annotation { "Feature Type Name" : "Feature", "Feature Type Description" : "" }
export const myFeature = defineFeature(function(context is Context, id is Id, definition is map)
    precondition{}
    {
        {
            var Q0;
            Q0=qCreatedBy(makeId("Front.planeOp"),FACE);
            var sketch = newSketch(context, id + "F0", { "sketchPlane" : qUnion([Q0])});
            skLineSegment(sketch, "E0", {"start": v(0, 0) * mm, "end": v(-50.92, 0) * mm, "construction": true});
            skLineSegment(sketch, "E1", {"start": v(-59.44, 28.53) * mm, "end": v(-47.38, 28.53) * mm});
            skLineSegment(sketch, "E2", {"start": v(-47.38, 28.53) * mm, "end": v(-46.97, 28.2) * mm});
            skLineSegment(sketch, "E3", {"start": v(-46.97, 28.2) * mm, "end": v(-46.4, 28.2) * mm});
            skLineSegment(sketch, "E4", {"start": v(-46.4, 28.2) * mm, "end": v(-46.08, 27.63) * mm});
            skLineSegment(sketch, "E5", {"start": v(-46.08, 27.63) * mm, "end": v(-45.23, 27.63) * mm});
            skLineSegment(sketch, "E6", {"start": v(-45.23, 27.63) * mm, "end": v(-44.93, 27.95) * mm});
            skLineSegment(sketch, "E7", {"start": v(-44.93, 27.95) * mm, "end": v(-41.43, 27.95) * mm});
            skLineSegment(sketch, "E8", {"start": v(-41.43, 27.95) * mm, "end": v(-38.99, 27.4) * mm});
            skLineSegment(sketch, "E9", {"start": v(-38.99, 27.4) * mm, "end": v(-34.59, 27.4) * mm});
            skLineSegment(sketch, "E10", {"start": v(-34.59, 27.4) * mm, "end": v(-21.47, 25.81) * mm});
            skLineSegment(sketch, "E11", {"start": v(-21.47, 25.81) * mm, "end": v(-21.47, 24.59) * mm});
            skLineSegment(sketch, "E12", {"start": v(-21.47, 24.59) * mm, "end": v(-21.11, 24.59) * mm});
            skLineSegment(sketch, "E13", {"start": v(-21.11, 24.59) * mm, "end": v(-21.11, 25.78) * mm});
            skLineSegment(sketch, "E14", {"start": v(-21.11, 25.78) * mm, "end": v(-7.6, 24.55) * mm});
            skLineSegment(sketch, "E15", {"start": v(-7.6, 24.55) * mm, "end": v(-7.6, 23.89) * mm});
            skLineSegment(sketch, "E16", {"start": v(-7.6, 23.89) * mm, "end": v(-8.15, 23.89) * mm});
            skLineSegment(sketch, "E17", {"start": v(-8.15, 23.89) * mm, "end": v(-8.15, 21.86) * mm});
            skLineSegment(sketch, "E18", {"start": v(-8.15, 21.86) * mm, "end": v(-7.6, 21.86) * mm});
            skLineSegment(sketch, "E19", {"start": v(-7.6, 21.86) * mm, "end": v(-7.6, 21.05) * mm});
            skLineSegment(sketch, "E20", {"start": v(-7.6, 21.05) * mm, "end": v(-21.1, 20.83) * mm});
            skLineSegment(sketch, "E21", {"start": v(-21.1, 20.83) * mm, "end": v(-21.13, 22.18) * mm});
            skLineSegment(sketch, "E22", {"start": v(-21.13, 22.18) * mm, "end": v(-21.48, 22.18) * mm});
            skLineSegment(sketch, "E23", {"start": v(-21.48, 22.18) * mm, "end": v(-21.48, 21.12) * mm});
            skLineSegment(sketch, "E24", {"start": v(-21.48, 21.12) * mm, "end": v(-21.7, 20.86) * mm});
            skLineSegment(sketch, "E25", {"start": v(-21.7, 20.86) * mm, "end": v(-22.73, 20.86) * mm});
            skLineSegment(sketch, "E26", {"start": v(-22.73, 20.86) * mm, "end": v(-22.73, 20.7) * mm});
            skLineSegment(sketch, "E27", {"start": v(-22.73, 20.7) * mm, "end": v(-18.14, 17.09) * mm});
            skLineSegment(sketch, "E28", {"start": v(-18.14, 17.09) * mm, "end": v(-16.15, 17.09) * mm});
            skLineSegment(sketch, "E29", {"start": v(-16.15, 17.09) * mm, "end": v(-0.56, 15.1) * mm});
            skLineSegment(sketch, "E30", {"start": v(-0.56, 15.1) * mm, "end": v(-0.54, 13.68) * mm});
            skLineSegment(sketch, "E31", {"start": v(-0.54, 13.68) * mm, "end": v(-0.25, 13.68) * mm});
            skLineSegment(sketch, "E32", {"start": v(-0.25, 13.68) * mm, "end": v(-0.27, 15.02) * mm});
            skLineSegment(sketch, "E33", {"start": v(-0.27, 15.02) * mm, "end": v(16.38, 13.51) * mm});
            skLineSegment(sketch, "E34", {"start": v(16.38, 13.51) * mm, "end": v(16.38, 12.7) * mm});
            skLineSegment(sketch, "E35", {"start": v(16.38, 12.7) * mm, "end": v(15.82, 12.7) * mm});
            skLineSegment(sketch, "E36", {"start": v(15.82, 12.7) * mm, "end": v(15.86, 10.38) * mm});
            skLineSegment(sketch, "E37", {"start": v(15.86, 10.38) * mm, "end": v(16.35, 10.38) * mm});
            skLineSegment(sketch, "E38", {"start": v(16.35, 10.38) * mm, "end": v(16.37, 9.4) * mm});
            skLineSegment(sketch, "E39", {"start": v(16.37, 9.4) * mm, "end": v(-0.25, 9.13) * mm});
            skLineSegment(sketch, "E40", {"start": v(-0.25, 9.13) * mm, "end": v(-0.28, 10.88) * mm});
            skLineSegment(sketch, "E41", {"start": v(-0.28, 10.88) * mm, "end": v(-0.54, 10.88) * mm});
            skLineSegment(sketch, "E42", {"start": v(-0.54, 10.88) * mm, "end": v(-0.54, 9.14) * mm});
            skLineSegment(sketch, "E43", {"start": v(-0.54, 9.14) * mm, "end": v(-8.2, 9.01) * mm});
            skLineSegment(sketch, "E44", {"start": v(-8.2, 9.01) * mm, "end": v(-8.2, 8.86) * mm});
            skLineSegment(sketch, "E45", {"start": v(-8.2, 8.86) * mm, "end": v(-7.44, 8.32) * mm});
            skArc(sketch, "E46", {"start": v(-3.59, 6.94) * mm, "mid": v(-5.48, 7.72) * mm, "end": v(-7.44, 8.32) * mm});
            skFitSpline(sketch, "E47", {"points": [v(-3.59, 6.94) * mm, v(-0.35, 6.94) * mm, v(7.38, 6.77) * mm, v(22.07, 6.1) * mm, v(35.41, 5.21) * mm, v(54.7, 3.45) * mm, v(59.39, 2.97) * mm], "startDerivative": vector(30.77, 0.14) * mm, "endDerivative": vector(31.87, -3.28) * mm});
            skLineSegment(sketch, "E48", {"start": v(59.39, 2.97) * mm, "end": v(60.15, 3.97) * mm});
            skArc(sketch, "E49", {"start": v(69.05, 3.31) * mm, "mid": v(64.61, 3.8) * mm, "end": v(60.15, 3.97) * mm});
            skLineSegment(sketch, "E50", {"start": v(69.05, 3.31) * mm, "end": v(67.9, 2.36) * mm});
            skLineSegment(sketch, "E51", {"start": v(67.9, 2.36) * mm, "end": v(64.73, 2.36) * mm});
            skArc(sketch, "E52", {"start": v(65.12, 0) * mm, "mid": v(65.03, 1.2) * mm, "end": v(64.73, 2.36) * mm});
            skLineSegment(sketch, "E53", {"start": v(-9.54, 23.56) * mm, "end": v(-9.54, 22.25) * mm});
            skLineSegment(sketch, "E54", {"start": v(-9.54, 22.25) * mm, "end": v(-13.93, 22.34) * mm});
            skLineSegment(sketch, "E55", {"start": v(-13.93, 22.34) * mm, "end": v(-13.9, 23.67) * mm});
            skLineSegment(sketch, "E56", {"start": v(-13.9, 23.67) * mm, "end": v(-9.54, 23.56) * mm});
            skLineSegment(sketch, "E57", {"start": v(-59.44, 28.53) * mm, "end": v(-59.44, 26.8) * mm});
            skLineSegment(sketch, "E58", {"start": v(-59.44, 26.8) * mm, "end": v(-59, 26.48) * mm});
            skLineSegment(sketch, "E59", {"start": v(-59, 26.48) * mm, "end": v(-58.94, 22.25) * mm});
            skLineSegment(sketch, "E60", {"start": v(-58.94, 22.25) * mm, "end": v(-59.44, 21.63) * mm});
            skLineSegment(sketch, "E61", {"start": v(-59.44, 21.63) * mm, "end": v(-59.47, 19.98) * mm});
            skLineSegment(sketch, "E62", {"start": v(-59.47, 19.98) * mm, "end": v(-47.36, 19.98) * mm});
            skLineSegment(sketch, "E63", {"start": v(-47.36, 19.98) * mm, "end": v(-47.03, 20.38) * mm});
            skLineSegment(sketch, "E64", {"start": v(-47.03, 20.38) * mm, "end": v(-46.32, 20.36) * mm});
            skLineSegment(sketch, "E65", {"start": v(-46.32, 20.36) * mm, "end": v(-45.77, 21.66) * mm});
            skLineSegment(sketch, "E66", {"start": v(-45.77, 21.66) * mm, "end": v(-45.07, 21.64) * mm});
            skLineSegment(sketch, "E67", {"start": v(-45.07, 21.64) * mm, "end": v(-45.04, 19.83) * mm});
            skLineSegment(sketch, "E68", {"start": v(-45.04, 19.83) * mm, "end": v(-44.78, 19.57) * mm});
            skLineSegment(sketch, "E69", {"start": v(-44.78, 19.57) * mm, "end": v(-41.37, 19.5) * mm});
            skLineSegment(sketch, "E70", {"start": v(-41.37, 19.5) * mm, "end": v(-40.25, 20.53) * mm});
            skLineSegment(sketch, "E71", {"start": v(-40.25, 20.53) * mm, "end": v(-33.73, 20.53) * mm});
            skLineSegment(sketch, "E72", {"start": v(-33.73, 20.53) * mm, "end": v(-33.68, 17.4) * mm});
            skLineSegment(sketch, "E73", {"start": v(-33.68, 17.4) * mm, "end": v(-39.86, 17.3) * mm});
            skLineSegment(sketch, "E74", {"start": v(-39.86, 17.3) * mm, "end": v(-40.9, 17.79) * mm});
            skLineSegment(sketch, "E75", {"start": v(-40.9, 17.79) * mm, "end": v(-41.73, 17.8) * mm});
            skLineSegment(sketch, "E76", {"start": v(-41.73, 17.8) * mm, "end": v(-41.99, 18.08) * mm});
            skLineSegment(sketch, "E77", {"start": v(-41.99, 18.08) * mm, "end": v(-55.95, 18.08) * mm});
            skLineSegment(sketch, "E78", {"start": v(-55.95, 18.08) * mm, "end": v(-56.22, 17.8) * mm});
            skLineSegment(sketch, "E79", {"start": v(-56.22, 17.8) * mm, "end": v(-56.2, 16.23) * mm});
            skLineSegment(sketch, "E80", {"start": v(-56.2, 16.23) * mm, "end": v(-55.86, 15.92) * mm});
            skLineSegment(sketch, "E81", {"start": v(-55.86, 15.92) * mm, "end": v(-55.77, 10.73) * mm});
            skLineSegment(sketch, "E82", {"start": v(-55.77, 10.73) * mm, "end": v(-56.18, 10.26) * mm});
            skLineSegment(sketch, "E83", {"start": v(-56.18, 10.26) * mm, "end": v(-56.18, 8.68) * mm});
            skLineSegment(sketch, "E84", {"start": v(-56.18, 8.68) * mm, "end": v(-55.89, 8.3) * mm});
            skLineSegment(sketch, "E85", {"start": v(-55.89, 8.3) * mm, "end": v(-42.04, 8.3) * mm});
            skLineSegment(sketch, "E86", {"start": v(-42.04, 8.3) * mm, "end": v(-41.71, 8.68) * mm});
            skLineSegment(sketch, "E87", {"start": v(-41.71, 8.68) * mm, "end": v(-40.93, 8.66) * mm});
            skLineSegment(sketch, "E88", {"start": v(-40.93, 8.66) * mm, "end": v(-40.27, 10.14) * mm});
            skLineSegment(sketch, "E89", {"start": v(-40.27, 10.14) * mm, "end": v(-39.56, 10.12) * mm});
            skLineSegment(sketch, "E90", {"start": v(-39.56, 10.12) * mm, "end": v(-39.53, 8.18) * mm});
            skLineSegment(sketch, "E91", {"start": v(-39.53, 8.18) * mm, "end": v(-39.2, 7.85) * mm});
            skLineSegment(sketch, "E92", {"start": v(-39.2, 7.85) * mm, "end": v(-35.01, 7.92) * mm});
            skLineSegment(sketch, "E93", {"start": v(-35.01, 7.92) * mm, "end": v(-33.69, 8.84) * mm});
            skLineSegment(sketch, "E94", {"start": v(-33.69, 8.84) * mm, "end": v(-33.65, 6.55) * mm});
            skLineSegment(sketch, "E95", {"start": v(-33.65, 6.55) * mm, "end": v(-34.72, 5.87) * mm});
            skArc(sketch, "E96", {"start": v(-34.72, 5.87) * mm, "mid": v(-39.46, 5.43) * mm, "end": v(-44.17, 4.85) * mm});
            skLineSegment(sketch, "E97", {"start": v(-44.17, 4.85) * mm, "end": v(-45.81, 5.4) * mm});
            skLineSegment(sketch, "E98", {"start": v(-45.81, 5.4) * mm, "end": v(-50.78, 5.4) * mm});
            skLineSegment(sketch, "E99", {"start": v(-50.78, 5.4) * mm, "end": v(-50.78, 4.85) * mm});
            skLineSegment(sketch, "E100", {"start": v(-50.78, 4.85) * mm, "end": v(-49.68, 4.3) * mm});
            skLineSegment(sketch, "E101", {"start": v(-49.68, 4.3) * mm, "end": v(-50.4, 4.15) * mm});
            skArc(sketch, "E102", {"start": v(-50.4, 4.15) * mm, "mid": v(-50.8, 2.1) * mm, "end": v(-50.92, 0) * mm});
            skLineSegment(sketch, "E103", {"start": v(-55.97, 26.17) * mm, "end": v(-53.15, 26.17) * mm});
            skLineSegment(sketch, "E104", {"start": v(-53.15, 26.17) * mm, "end": v(-53.15, 22.48) * mm});
            skLineSegment(sketch, "E105", {"start": v(-53.15, 22.48) * mm, "end": v(-56, 22.48) * mm});
            skLineSegment(sketch, "E106", {"start": v(-56, 22.48) * mm, "end": v(-55.97, 26.17) * mm});
            skLineSegment(sketch, "E107", {"start": v(-52.12, 15.28) * mm, "end": v(-48.82, 15.28) * mm});
            skLineSegment(sketch, "E108", {"start": v(-48.82, 15.28) * mm, "end": v(-48.82, 11.05) * mm});
            skLineSegment(sketch, "E109", {"start": v(-48.82, 11.05) * mm, "end": v(-52.12, 11.05) * mm});
            skLineSegment(sketch, "E110", {"start": v(-52.12, 11.05) * mm, "end": v(-52.12, 15.28) * mm});
            skLineSegment(sketch, "E111", {"start": v(8.86, 12.6) * mm, "end": v(14.27, 12.35) * mm});
            skLineSegment(sketch, "E112", {"start": v(14.27, 12.35) * mm, "end": v(14.3, 10.92) * mm});
            skLineSegment(sketch, "E113", {"start": v(14.3, 10.92) * mm, "end": v(8.89, 11.02) * mm});
            skLineSegment(sketch, "E114", {"start": v(8.89, 11.02) * mm, "end": v(8.86, 12.6) * mm});
            skLineSegment(sketch, "E115.MirrorCS", {"start": v(-0.28, -10.88) * mm, "end": v(-0.54, -10.88) * mm});
            skLineSegment(sketch, "E116.MirrorCS", {"start": v(-21.13, -22.18) * mm, "end": v(-21.48, -22.18) * mm});
            skLineSegment(sketch, "E117.MirrorCS", {"start": v(-0.54, -13.68) * mm, "end": v(-0.25, -13.68) * mm});
            skLineSegment(sketch, "E118.MirrorCS", {"start": v(-0.25, -9.13) * mm, "end": v(-0.28, -10.88) * mm});
            skLineSegment(sketch, "E119.MirrorCS", {"start": v(-0.56, -15.1) * mm, "end": v(-0.54, -13.68) * mm});
            skLineSegment(sketch, "E120.MirrorCS", {"start": v(-8.15, -21.86) * mm, "end": v(-7.6, -21.86) * mm});
            skLineSegment(sketch, "E121.MirrorCS", {"start": v(-21.48, -22.18) * mm, "end": v(-21.48, -21.12) * mm});
            skLineSegment(sketch, "E122.MirrorCS", {"start": v(-0.25, -13.68) * mm, "end": v(-0.27, -15.02) * mm});
            skLineSegment(sketch, "E123.MirrorCS", {"start": v(-21.7, -20.86) * mm, "end": v(-22.73, -20.86) * mm});
            skLineSegment(sketch, "E124.MirrorCS", {"start": v(-0.54, -10.88) * mm, "end": v(-0.54, -9.14) * mm});
            skLineSegment(sketch, "E125.MirrorCS", {"start": v(-55.95, -18.08) * mm, "end": v(-56.22, -17.8) * mm});
            skLineSegment(sketch, "E126.MirrorCS", {"start": v(16.35, -10.38) * mm, "end": v(16.37, -9.4) * mm});
            skLineSegment(sketch, "E127.MirrorCS", {"start": v(15.86, -10.38) * mm, "end": v(16.35, -10.38) * mm});
            skLineSegment(sketch, "E128.MirrorCS", {"start": v(-21.1, -20.83) * mm, "end": v(-21.13, -22.18) * mm});
            skLineSegment(sketch, "E129.MirrorCS", {"start": v(-56.22, -17.8) * mm, "end": v(-56.2, -16.23) * mm});
            skLineSegment(sketch, "E130.MirrorCS", {"start": v(-47.36, -19.98) * mm, "end": v(-47.03, -20.38) * mm});
            skLineSegment(sketch, "E131.MirrorCS", {"start": v(-45.04, -19.83) * mm, "end": v(-44.78, -19.57) * mm});
            skLineSegment(sketch, "E132.MirrorCS", {"start": v(-56.18, -8.68) * mm, "end": v(-55.89, -8.3) * mm});
            skLineSegment(sketch, "E133.MirrorCS", {"start": v(15.82, -12.7) * mm, "end": v(15.86, -10.38) * mm});
            skLineSegment(sketch, "E134.MirrorCS", {"start": v(-56.2, -16.23) * mm, "end": v(-55.86, -15.92) * mm});
            skLineSegment(sketch, "E135.MirrorCS", {"start": v(59.39, -2.97) * mm, "end": v(60.15, -3.97) * mm});
            skLineSegment(sketch, "E136.MirrorCS", {"start": v(-39.53, -8.18) * mm, "end": v(-39.2, -7.85) * mm});
            skLineSegment(sketch, "E137.MirrorCS", {"start": v(-21.48, -21.12) * mm, "end": v(-21.7, -20.86) * mm});
            skLineSegment(sketch, "E138.MirrorCS", {"start": v(-8.15, -23.89) * mm, "end": v(-8.15, -21.86) * mm});
            skLineSegment(sketch, "E139.MirrorCS", {"start": v(-7.6, -21.86) * mm, "end": v(-7.6, -21.05) * mm});
            skLineSegment(sketch, "E140.MirrorCS", {"start": v(-22.73, -20.86) * mm, "end": v(-22.73, -20.7) * mm});
            skLineSegment(sketch, "E141.MirrorCS", {"start": v(-45.07, -21.64) * mm, "end": v(-45.04, -19.83) * mm});
            skLineSegment(sketch, "E142.MirrorCS", {"start": v(-56.18, -10.26) * mm, "end": v(-56.18, -8.68) * mm});
            skLineSegment(sketch, "E143.MirrorCS", {"start": v(-46.32, -20.36) * mm, "end": v(-45.77, -21.66) * mm});
            skArc(sketch, "E144.MirrorCS", {"start": v(-3.59, -6.94) * mm, "mid": v(-5.48, -7.72) * mm, "end": v(-7.44, -8.32) * mm});
            skLineSegment(sketch, "E145.MirrorCS", {"start": v(-8.2, -8.86) * mm, "end": v(-7.44, -8.32) * mm});
            skLineSegment(sketch, "E146.MirrorCS", {"start": v(-40.9, -17.79) * mm, "end": v(-41.73, -17.8) * mm});
            skLineSegment(sketch, "E147.MirrorCS", {"start": v(-45.77, -21.66) * mm, "end": v(-45.07, -21.64) * mm});
            skLineSegment(sketch, "E148.MirrorCS", {"start": v(16.38, -13.51) * mm, "end": v(16.38, -12.7) * mm});
            skLineSegment(sketch, "E149.MirrorCS", {"start": v(-7.6, -23.89) * mm, "end": v(-8.15, -23.89) * mm});
            skLineSegment(sketch, "E150.MirrorCS", {"start": v(-47.03, -20.38) * mm, "end": v(-46.32, -20.36) * mm});
            skLineSegment(sketch, "E151.MirrorCS", {"start": v(-8.2, -9.01) * mm, "end": v(-8.2, -8.86) * mm});
            skLineSegment(sketch, "E152.MirrorCS", {"start": v(-41.73, -17.8) * mm, "end": v(-41.99, -18.08) * mm});
            skLineSegment(sketch, "E153.MirrorCS", {"start": v(-21.47, -24.59) * mm, "end": v(-21.11, -24.59) * mm});
            skLineSegment(sketch, "E154.MirrorCS", {"start": v(-40.27, -10.14) * mm, "end": v(-39.56, -10.12) * mm});
            skLineSegment(sketch, "E155.MirrorCS", {"start": v(16.38, -12.7) * mm, "end": v(15.82, -12.7) * mm});
            skLineSegment(sketch, "E156.MirrorCS", {"start": v(-39.86, -17.3) * mm, "end": v(-40.9, -17.79) * mm});
            skLineSegment(sketch, "E157.MirrorCS", {"start": v(-46.97, -28.2) * mm, "end": v(-46.4, -28.2) * mm});
            skLineSegment(sketch, "E158.MirrorCS", {"start": v(-45.23, -27.63) * mm, "end": v(-44.93, -27.95) * mm});
            skLineSegment(sketch, "E159.MirrorCS", {"start": v(-33.69, -8.84) * mm, "end": v(-33.65, -6.55) * mm});
            skLineSegment(sketch, "E160.MirrorCS", {"start": v(-52.12, -11.05) * mm, "end": v(-52.12, -15.28) * mm});
            skLineSegment(sketch, "E161.MirrorCS", {"start": v(-9.54, -22.25) * mm, "end": v(-13.93, -22.34) * mm});
            skArc(sketch, "E162.MirrorCS", {"start": v(-50.4, -4.15) * mm, "mid": v(-50.8, -2.1) * mm, "end": v(-50.92, 0) * mm});
            skLineSegment(sketch, "E163.MirrorCS", {"start": v(-42.04, -8.3) * mm, "end": v(-41.71, -8.68) * mm});
            skLineSegment(sketch, "E164.MirrorCS", {"start": v(-41.37, -19.5) * mm, "end": v(-40.25, -20.53) * mm});
            skLineSegment(sketch, "E165.MirrorCS", {"start": v(-7.6, -24.55) * mm, "end": v(-7.6, -23.89) * mm});
            skLineSegment(sketch, "E166.MirrorCS", {"start": v(-44.78, -19.57) * mm, "end": v(-41.37, -19.5) * mm});
            skLineSegment(sketch, "E167.MirrorCS", {"start": v(-49.68, -4.3) * mm, "end": v(-50.4, -4.15) * mm});
            skLineSegment(sketch, "E168.MirrorCS", {"start": v(-9.54, -23.56) * mm, "end": v(-9.54, -22.25) * mm});
            skLineSegment(sketch, "E169.MirrorCS", {"start": v(-33.65, -6.55) * mm, "end": v(-34.72, -5.87) * mm});
            skLineSegment(sketch, "E170.MirrorCS", {"start": v(-35.01, -7.92) * mm, "end": v(-33.69, -8.84) * mm});
            skLineSegment(sketch, "E171.MirrorCS", {"start": v(-48.82, -11.05) * mm, "end": v(-52.12, -11.05) * mm});
            skLineSegment(sketch, "E172.MirrorCS", {"start": v(-59.44, -21.63) * mm, "end": v(-59.47, -19.98) * mm});
            skLineSegment(sketch, "E173.MirrorCS", {"start": v(-21.11, -24.59) * mm, "end": v(-21.11, -25.78) * mm});
            skLineSegment(sketch, "E174.MirrorCS", {"start": v(-13.93, -22.34) * mm, "end": v(-13.9, -23.67) * mm});
            skLineSegment(sketch, "E175.MirrorCS", {"start": v(-55.97, -26.17) * mm, "end": v(-53.15, -26.17) * mm});
            skLineSegment(sketch, "E176.MirrorCS", {"start": v(-41.71, -8.68) * mm, "end": v(-40.93, -8.66) * mm});
            skLineSegment(sketch, "E177.MirrorCS", {"start": v(-50.78, -4.85) * mm, "end": v(-49.68, -4.3) * mm});
            skLineSegment(sketch, "E178.MirrorCS", {"start": v(-55.77, -10.73) * mm, "end": v(-56.18, -10.26) * mm});
            skLineSegment(sketch, "E179.MirrorCS", {"start": v(-59, -26.48) * mm, "end": v(-58.94, -22.25) * mm});
            skLineSegment(sketch, "E180.MirrorCS", {"start": v(69.05, -3.31) * mm, "end": v(67.9, -2.36) * mm});
            skLineSegment(sketch, "E181.MirrorCS", {"start": v(-22.73, -20.7) * mm, "end": v(-18.14, -17.09) * mm});
            skLineSegment(sketch, "E182.MirrorCS", {"start": v(-52.12, -15.28) * mm, "end": v(-48.82, -15.28) * mm});
            skLineSegment(sketch, "E183.MirrorCS", {"start": v(8.89, -11.02) * mm, "end": v(8.86, -12.6) * mm});
            skLineSegment(sketch, "E184.MirrorCS", {"start": v(-59.44, -28.53) * mm, "end": v(-59.44, -26.8) * mm});
            skLineSegment(sketch, "E185.MirrorCS", {"start": v(-18.14, -17.09) * mm, "end": v(-16.15, -17.09) * mm});
            skLineSegment(sketch, "E186.MirrorCS", {"start": v(-45.81, -5.4) * mm, "end": v(-50.78, -5.4) * mm});
            skLineSegment(sketch, "E187.MirrorCS", {"start": v(-58.94, -22.25) * mm, "end": v(-59.44, -21.63) * mm});
            skLineSegment(sketch, "E188.MirrorCS", {"start": v(67.9, -2.36) * mm, "end": v(64.73, -2.36) * mm});
            skLineSegment(sketch, "E189.MirrorCS", {"start": v(-39.2, -7.85) * mm, "end": v(-35.01, -7.92) * mm});
            skLineSegment(sketch, "E190.MirrorCS", {"start": v(-44.17, -4.85) * mm, "end": v(-45.81, -5.4) * mm});
            skLineSegment(sketch, "E191.MirrorCS", {"start": v(-48.82, -15.28) * mm, "end": v(-48.82, -11.05) * mm});
            skLineSegment(sketch, "E192.MirrorCS", {"start": v(14.27, -12.35) * mm, "end": v(14.3, -10.92) * mm});
            skLineSegment(sketch, "E193.MirrorCS", {"start": v(-13.9, -23.67) * mm, "end": v(-9.54, -23.56) * mm});
            skLineSegment(sketch, "E194.MirrorCS", {"start": v(-53.15, -26.17) * mm, "end": v(-53.15, -22.48) * mm});
            skLineSegment(sketch, "E195.MirrorCS", {"start": v(-33.73, -20.53) * mm, "end": v(-33.68, -17.4) * mm});
            skLineSegment(sketch, "E196.MirrorCS", {"start": v(-56, -22.48) * mm, "end": v(-55.97, -26.17) * mm});
            skLineSegment(sketch, "E197.MirrorCS", {"start": v(-40.93, -8.66) * mm, "end": v(-40.27, -10.14) * mm});
            skLineSegment(sketch, "E198.MirrorCS", {"start": v(-39.56, -10.12) * mm, "end": v(-39.53, -8.18) * mm});
            skLineSegment(sketch, "E199.MirrorCS", {"start": v(-50.78, -5.4) * mm, "end": v(-50.78, -4.85) * mm});
            skLineSegment(sketch, "E200.MirrorCS", {"start": v(-53.15, -22.48) * mm, "end": v(-56, -22.48) * mm});
            skLineSegment(sketch, "E201.MirrorCS", {"start": v(-59.44, -26.8) * mm, "end": v(-59, -26.48) * mm});
            skLineSegment(sketch, "E202.MirrorCS", {"start": v(-21.47, -25.81) * mm, "end": v(-21.47, -24.59) * mm});
            skLineSegment(sketch, "E203.MirrorCS", {"start": v(-44.93, -27.95) * mm, "end": v(-41.43, -27.95) * mm});
            skLineSegment(sketch, "E204.MirrorCS", {"start": v(-47.38, -28.53) * mm, "end": v(-46.97, -28.2) * mm});
            skLineSegment(sketch, "E205.MirrorCS", {"start": v(-46.08, -27.63) * mm, "end": v(-45.23, -27.63) * mm});
            skLineSegment(sketch, "E206.MirrorCS", {"start": v(-46.4, -28.2) * mm, "end": v(-46.08, -27.63) * mm});
            skLineSegment(sketch, "E207.MirrorCS", {"start": v(-41.43, -27.95) * mm, "end": v(-38.99, -27.4) * mm});
            skArc(sketch, "E208.MirrorCS", {"start": v(65.12, 0) * mm, "mid": v(65.03, -1.2) * mm, "end": v(64.73, -2.36) * mm});
            skLineSegment(sketch, "E209.MirrorCS", {"start": v(-0.54, -9.14) * mm, "end": v(-8.2, -9.01) * mm});
            skLineSegment(sketch, "E210.MirrorCS", {"start": v(-59.47, -19.98) * mm, "end": v(-47.36, -19.98) * mm});
            skLineSegment(sketch, "E211.MirrorCS", {"start": v(-21.11, -25.78) * mm, "end": v(-7.6, -24.55) * mm});
            skLineSegment(sketch, "E212.MirrorCS", {"start": v(-55.89, -8.3) * mm, "end": v(-42.04, -8.3) * mm});
            skFitSpline(sketch, "E213.MirrorCS", {"points": [v(-3.59, -6.94) * mm, v(-0.35, -6.94) * mm, v(7.38, -6.77) * mm, v(22.07, -6.1) * mm, v(35.41, -5.21) * mm, v(54.7, -3.45) * mm, v(59.39, -2.97) * mm], "startDerivative": vector(30.77, -0.14) * mm, "endDerivative": vector(31.87, 3.28) * mm});
            skLineSegment(sketch, "E214.MirrorCS", {"start": v(8.86, -12.6) * mm, "end": v(14.27, -12.35) * mm});
            skLineSegment(sketch, "E215.MirrorCS", {"start": v(-16.15, -17.09) * mm, "end": v(-0.56, -15.1) * mm});
            skLineSegment(sketch, "E216.MirrorCS", {"start": v(-41.99, -18.08) * mm, "end": v(-55.95, -18.08) * mm});
            skLineSegment(sketch, "E217.MirrorCS", {"start": v(16.37, -9.4) * mm, "end": v(-0.25, -9.13) * mm});
            skLineSegment(sketch, "E218.MirrorCS", {"start": v(-7.6, -21.05) * mm, "end": v(-21.1, -20.83) * mm});
            skLineSegment(sketch, "E219.MirrorCS", {"start": v(-40.25, -20.53) * mm, "end": v(-33.73, -20.53) * mm});
            skLineSegment(sketch, "E220.MirrorCS", {"start": v(-33.68, -17.4) * mm, "end": v(-39.86, -17.3) * mm});
            skLineSegment(sketch, "E221.MirrorCS", {"start": v(-34.59, -27.4) * mm, "end": v(-21.47, -25.81) * mm});
            skLineSegment(sketch, "E222.MirrorCS", {"start": v(-38.99, -27.4) * mm, "end": v(-34.59, -27.4) * mm});
            skLineSegment(sketch, "E223.MirrorCS", {"start": v(14.3, -10.92) * mm, "end": v(8.89, -11.02) * mm});
            skLineSegment(sketch, "E224.MirrorCS", {"start": v(-59.44, -28.53) * mm, "end": v(-47.38, -28.53) * mm});
            skLineSegment(sketch, "E225.MirrorCS", {"start": v(-55.86, -15.92) * mm, "end": v(-55.77, -10.73) * mm});
            skLineSegment(sketch, "E226.MirrorCS", {"start": v(-0.27, -15.02) * mm, "end": v(16.38, -13.51) * mm});
            skArc(sketch, "E227.MirrorCS", {"start": v(69.05, -3.31) * mm, "mid": v(64.61, -3.8) * mm, "end": v(60.15, -3.97) * mm});
            skArc(sketch, "E228.MirrorCS", {"start": v(-34.72, -5.87) * mm, "mid": v(-39.46, -5.43) * mm, "end": v(-44.17, -4.85) * mm});
            skSolve(sketch);
        }
        {
            var Q0;
            Q0=makeQuery(id+"F0.imprint","IMPRINT",FACE,{"disambiguationData":[TD([[makeQuery(id+"F0.imprint","IMPRINT",EDGE,{"derivedFrom":sQuery(id+"F0.wireOp",EDGE,"E1")}),-1.0]])]});
            extrude(context, id + "F1", {"entities" : qUnion([Q0]), "depth" : 2 * mm, "offsetDistance" : 25 * mm});
        }
        {
            var Q0;
            Q0=makeQuery(id+"F1.opExtrude","SWEPT_BODY",BODY,{"disambiguationData":[OSD([sQuery(id+"F0.wireOp",EDGE,"E1"),sQuery(id+"F0.wireOp",EDGE,"E2"),sQuery(id+"F0.wireOp",EDGE,"E3"),sQuery(id+"F0.wireOp",EDGE,"E4"),sQuery(id+"F0.wireOp",EDGE,"E5"),sQuery(id+"F0.wireOp",EDGE,"E6"),sQuery(id+"F0.wireOp",EDGE,"E7"),sQuery(id+"F0.wireOp",EDGE,"E8"),sQuery(id+"F0.wireOp",EDGE,"E9"),sQuery(id+"F0.wireOp",EDGE,"E10"),sQuery(id+"F0.wireOp",EDGE,"E11"),sQuery(id+"F0.wireOp",EDGE,"E12"),sQuery(id+"F0.wireOp",EDGE,"E13"),sQuery(id+"F0.wireOp",EDGE,"E14"),sQuery(id+"F0.wireOp",EDGE,"E15"),sQuery(id+"F0.wireOp",EDGE,"E16"),sQuery(id+"F0.wireOp",EDGE,"E17"),sQuery(id+"F0.wireOp",EDGE,"E18"),sQuery(id+"F0.wireOp",EDGE,"E19"),sQuery(id+"F0.wireOp",EDGE,"E20"),sQuery(id+"F0.wireOp",EDGE,"E21"),sQuery(id+"F0.wireOp",EDGE,"E22"),sQuery(id+"F0.wireOp",EDGE,"E23"),sQuery(id+"F0.wireOp",EDGE,"E24"),sQuery(id+"F0.wireOp",EDGE,"E25"),sQuery(id+"F0.wireOp",EDGE,"E26"),sQuery(id+"F0.wireOp",EDGE,"E27"),sQuery(id+"F0.wireOp",EDGE,"E28"),sQuery(id+"F0.wireOp",EDGE,"E29"),sQuery(id+"F0.wireOp",EDGE,"E30"),sQuery(id+"F0.wireOp",EDGE,"E31"),sQuery(id+"F0.wireOp",EDGE,"E32"),sQuery(id+"F0.wireOp",EDGE,"E33"),sQuery(id+"F0.wireOp",EDGE,"E34"),sQuery(id+"F0.wireOp",EDGE,"E35"),sQuery(id+"F0.wireOp",EDGE,"E36"),sQuery(id+"F0.wireOp",EDGE,"E37"),sQuery(id+"F0.wireOp",EDGE,"E38"),sQuery(id+"F0.wireOp",EDGE,"E39"),sQuery(id+"F0.wireOp",EDGE,"E40"),sQuery(id+"F0.wireOp",EDGE,"E41"),sQuery(id+"F0.wireOp",EDGE,"E42"),sQuery(id+"F0.wireOp",EDGE,"E43"),sQuery(id+"F0.wireOp",EDGE,"E44"),sQuery(id+"F0.wireOp",EDGE,"E45"),sQuery(id+"F0.wireOp",EDGE,"E46"),sQuery(id+"F0.wireOp",EDGE,"E47"),sQuery(id+"F0.wireOp",EDGE,"E48"),sQuery(id+"F0.wireOp",EDGE,"E49"),sQuery(id+"F0.wireOp",EDGE,"E50"),sQuery(id+"F0.wireOp",EDGE,"E51"),sQuery(id+"F0.wireOp",EDGE,"E52"),sQuery(id+"F0.wireOp",EDGE,"E53"),sQuery(id+"F0.wireOp",EDGE,"E54"),sQuery(id+"F0.wireOp",EDGE,"E55"),sQuery(id+"F0.wireOp",EDGE,"E56"),sQuery(id+"F0.wireOp",EDGE,"E57"),sQuery(id+"F0.wireOp",EDGE,"E58"),sQuery(id+"F0.wireOp",EDGE,"E59"),sQuery(id+"F0.wireOp",EDGE,"E60"),sQuery(id+"F0.wireOp",EDGE,"E61"),sQuery(id+"F0.wireOp",EDGE,"E62"),sQuery(id+"F0.wireOp",EDGE,"E63"),sQuery(id+"F0.wireOp",EDGE,"E64"),sQuery(id+"F0.wireOp",EDGE,"E65"),sQuery(id+"F0.wireOp",EDGE,"E66"),sQuery(id+"F0.wireOp",EDGE,"E67"),sQuery(id+"F0.wireOp",EDGE,"E68"),sQuery(id+"F0.wireOp",EDGE,"E69"),sQuery(id+"F0.wireOp",EDGE,"E70"),sQuery(id+"F0.wireOp",EDGE,"E71"),sQuery(id+"F0.wireOp",EDGE,"E72"),sQuery(id+"F0.wireOp",EDGE,"E73"),sQuery(id+"F0.wireOp",EDGE,"E74"),sQuery(id+"F0.wireOp",EDGE,"E75"),sQuery(id+"F0.wireOp",EDGE,"E76"),sQuery(id+"F0.wireOp",EDGE,"E77"),sQuery(id+"F0.wireOp",EDGE,"E78"),sQuery(id+"F0.wireOp",EDGE,"E79"),sQuery(id+"F0.wireOp",EDGE,"E80"),sQuery(id+"F0.wireOp",EDGE,"E81"),sQuery(id+"F0.wireOp",EDGE,"E82"),sQuery(id+"F0.wireOp",EDGE,"E83"),sQuery(id+"F0.wireOp",EDGE,"E84"),sQuery(id+"F0.wireOp",EDGE,"E85"),sQuery(id+"F0.wireOp",EDGE,"E86"),sQuery(id+"F0.wireOp",EDGE,"E87"),sQuery(id+"F0.wireOp",EDGE,"E88"),sQuery(id+"F0.wireOp",EDGE,"E89"),sQuery(id+"F0.wireOp",EDGE,"E90"),sQuery(id+"F0.wireOp",EDGE,"E91"),sQuery(id+"F0.wireOp",EDGE,"E92"),sQuery(id+"F0.wireOp",EDGE,"E93"),sQuery(id+"F0.wireOp",EDGE,"E94"),sQuery(id+"F0.wireOp",EDGE,"E95"),sQuery(id+"F0.wireOp",EDGE,"E96"),sQuery(id+"F0.wireOp",EDGE,"E97"),sQuery(id+"F0.wireOp",EDGE,"E98"),sQuery(id+"F0.wireOp",EDGE,"E99"),sQuery(id+"F0.wireOp",EDGE,"E100"),sQuery(id+"F0.wireOp",EDGE,"E101"),sQuery(id+"F0.wireOp",EDGE,"E102"),sQuery(id+"F0.wireOp",EDGE,"E103"),sQuery(id+"F0.wireOp",EDGE,"E104"),sQuery(id+"F0.wireOp",EDGE,"E105"),sQuery(id+"F0.wireOp",EDGE,"E106"),sQuery(id+"F0.wireOp",EDGE,"E107"),sQuery(id+"F0.wireOp",EDGE,"E108"),sQuery(id+"F0.wireOp",EDGE,"E109"),sQuery(id+"F0.wireOp",EDGE,"E110"),sQuery(id+"F0.wireOp",EDGE,"E111"),sQuery(id+"F0.wireOp",EDGE,"E112"),sQuery(id+"F0.wireOp",EDGE,"E113"),sQuery(id+"F0.wireOp",EDGE,"E114"),sQuery(id+"F0.wireOp",EDGE,"E115.MirrorCS"),sQuery(id+"F0.wireOp",EDGE,"E116.MirrorCS"),sQuery(id+"F0.wireOp",EDGE,"E117.MirrorCS"),sQuery(id+"F0.wireOp",EDGE,"E118.MirrorCS"),sQuery(id+"F0.wireOp",EDGE,"E119.MirrorCS"),sQuery(id+"F0.wireOp",EDGE,"E120.MirrorCS"),sQuery(id+"F0.wireOp",EDGE,"E121.MirrorCS"),sQuery(id+"F0.wireOp",EDGE,"E122.MirrorCS"),sQuery(id+"F0.wireOp",EDGE,"E123.MirrorCS"),sQuery(id+"F0.wireOp",EDGE,"E124.MirrorCS"),sQuery(id+"F0.wireOp",EDGE,"E125.MirrorCS"),sQuery(id+"F0.wireOp",EDGE,"E126.MirrorCS"),sQuery(id+"F0.wireOp",EDGE,"E127.MirrorCS"),sQuery(id+"F0.wireOp",EDGE,"E128.MirrorCS"),sQuery(id+"F0.wireOp",EDGE,"E129.MirrorCS"),sQuery(id+"F0.wireOp",EDGE,"E130.MirrorCS"),sQuery(id+"F0.wireOp",EDGE,"E131.MirrorCS"),sQuery(id+"F0.wireOp",EDGE,"E132.MirrorCS"),sQuery(id+"F0.wireOp",EDGE,"E133.MirrorCS"),sQuery(id+"F0.wireOp",EDGE,"E134.MirrorCS"),sQuery(id+"F0.wireOp",EDGE,"E135.MirrorCS"),sQuery(id+"F0.wireOp",EDGE,"E136.MirrorCS"),sQuery(id+"F0.wireOp",EDGE,"E137.MirrorCS"),sQuery(id+"F0.wireOp",EDGE,"E138.MirrorCS"),sQuery(id+"F0.wireOp",EDGE,"E139.MirrorCS"),sQuery(id+"F0.wireOp",EDGE,"E140.MirrorCS"),sQuery(id+"F0.wireOp",EDGE,"E141.MirrorCS"),sQuery(id+"F0.wireOp",EDGE,"E142.MirrorCS"),sQuery(id+"F0.wireOp",EDGE,"E143.MirrorCS"),sQuery(id+"F0.wireOp",EDGE,"E144.MirrorCS"),sQuery(id+"F0.wireOp",EDGE,"E145.MirrorCS"),sQuery(id+"F0.wireOp",EDGE,"E146.MirrorCS"),sQuery(id+"F0.wireOp",EDGE,"E147.MirrorCS"),sQuery(id+"F0.wireOp",EDGE,"E148.MirrorCS"),sQuery(id+"F0.wireOp",EDGE,"E149.MirrorCS"),sQuery(id+"F0.wireOp",EDGE,"E150.MirrorCS"),sQuery(id+"F0.wireOp",EDGE,"E151.MirrorCS"),sQuery(id+"F0.wireOp",EDGE,"E152.MirrorCS"),sQuery(id+"F0.wireOp",EDGE,"E153.MirrorCS"),sQuery(id+"F0.wireOp",EDGE,"E154.MirrorCS"),sQuery(id+"F0.wireOp",EDGE,"E155.MirrorCS"),sQuery(id+"F0.wireOp",EDGE,"E156.MirrorCS"),sQuery(id+"F0.wireOp",EDGE,"E157.MirrorCS"),sQuery(id+"F0.wireOp",EDGE,"E158.MirrorCS"),sQuery(id+"F0.wireOp",EDGE,"E159.MirrorCS"),sQuery(id+"F0.wireOp",EDGE,"E160.MirrorCS"),sQuery(id+"F0.wireOp",EDGE,"E161.MirrorCS"),sQuery(id+"F0.wireOp",EDGE,"E162.MirrorCS"),sQuery(id+"F0.wireOp",EDGE,"E163.MirrorCS"),sQuery(id+"F0.wireOp",EDGE,"E164.MirrorCS"),sQuery(id+"F0.wireOp",EDGE,"E165.MirrorCS"),sQuery(id+"F0.wireOp",EDGE,"E166.MirrorCS"),sQuery(id+"F0.wireOp",EDGE,"E167.MirrorCS"),sQuery(id+"F0.wireOp",EDGE,"E168.MirrorCS"),sQuery(id+"F0.wireOp",EDGE,"E169.MirrorCS"),sQuery(id+"F0.wireOp",EDGE,"E170.MirrorCS"),sQuery(id+"F0.wireOp",EDGE,"E171.MirrorCS"),sQuery(id+"F0.wireOp",EDGE,"E172.MirrorCS"),sQuery(id+"F0.wireOp",EDGE,"E173.MirrorCS"),sQuery(id+"F0.wireOp",EDGE,"E174.MirrorCS"),sQuery(id+"F0.wireOp",EDGE,"E175.MirrorCS"),sQuery(id+"F0.wireOp",EDGE,"E176.MirrorCS"),sQuery(id+"F0.wireOp",EDGE,"E177.MirrorCS"),sQuery(id+"F0.wireOp",EDGE,"E178.MirrorCS"),sQuery(id+"F0.wireOp",EDGE,"E179.MirrorCS"),sQuery(id+"F0.wireOp",EDGE,"E180.MirrorCS"),sQuery(id+"F0.wireOp",EDGE,"E181.MirrorCS"),sQuery(id+"F0.wireOp",EDGE,"E182.MirrorCS"),sQuery(id+"F0.wireOp",EDGE,"E183.MirrorCS"),sQuery(id+"F0.wireOp",EDGE,"E184.MirrorCS"),sQuery(id+"F0.wireOp",EDGE,"E185.MirrorCS"),sQuery(id+"F0.wireOp",EDGE,"E186.MirrorCS"),sQuery(id+"F0.wireOp",EDGE,"E187.MirrorCS"),sQuery(id+"F0.wireOp",EDGE,"E188.MirrorCS"),sQuery(id+"F0.wireOp",EDGE,"E189.MirrorCS"),sQuery(id+"F0.wireOp",EDGE,"E190.MirrorCS"),sQuery(id+"F0.wireOp",EDGE,"E191.MirrorCS"),sQuery(id+"F0.wireOp",EDGE,"E192.MirrorCS"),sQuery(id+"F0.wireOp",EDGE,"E193.MirrorCS"),sQuery(id+"F0.wireOp",EDGE,"E194.MirrorCS"),sQuery(id+"F0.wireOp",EDGE,"E195.MirrorCS"),sQuery(id+"F0.wireOp",EDGE,"E196.MirrorCS"),sQuery(id+"F0.wireOp",EDGE,"E197.MirrorCS"),sQuery(id+"F0.wireOp",EDGE,"E198.MirrorCS"),sQuery(id+"F0.wireOp",EDGE,"E199.MirrorCS"),sQuery(id+"F0.wireOp",EDGE,"E200.MirrorCS"),sQuery(id+"F0.wireOp",EDGE,"E201.MirrorCS"),sQuery(id+"F0.wireOp",EDGE,"E202.MirrorCS"),sQuery(id+"F0.wireOp",EDGE,"E203.MirrorCS"),sQuery(id+"F0.wireOp",EDGE,"E204.MirrorCS"),sQuery(id+"F0.wireOp",EDGE,"E205.MirrorCS"),sQuery(id+"F0.wireOp",EDGE,"E206.MirrorCS"),sQuery(id+"F0.wireOp",EDGE,"E207.MirrorCS"),sQuery(id+"F0.wireOp",EDGE,"E208.MirrorCS"),sQuery(id+"F0.wireOp",EDGE,"E209.MirrorCS"),sQuery(id+"F0.wireOp",EDGE,"E210.MirrorCS"),sQuery(id+"F0.wireOp",EDGE,"E211.MirrorCS"),sQuery(id+"F0.wireOp",EDGE,"E212.MirrorCS"),sQuery(id+"F0.wireOp",EDGE,"E213.MirrorCS"),sQuery(id+"F0.wireOp",EDGE,"E214.MirrorCS"),sQuery(id+"F0.wireOp",EDGE,"E215.MirrorCS"),sQuery(id+"F0.wireOp",EDGE,"E216.MirrorCS"),sQuery(id+"F0.wireOp",EDGE,"E217.MirrorCS"),sQuery(id+"F0.wireOp",EDGE,"E218.MirrorCS"),sQuery(id+"F0.wireOp",EDGE,"E219.MirrorCS"),sQuery(id+"F0.wireOp",EDGE,"E220.MirrorCS"),sQuery(id+"F0.wireOp",EDGE,"E221.MirrorCS"),sQuery(id+"F0.wireOp",EDGE,"E222.MirrorCS"),sQuery(id+"F0.wireOp",EDGE,"E223.MirrorCS"),sQuery(id+"F0.wireOp",EDGE,"E224.MirrorCS"),sQuery(id+"F0.wireOp",EDGE,"E225.MirrorCS"),sQuery(id+"F0.wireOp",EDGE,"E226.MirrorCS"),sQuery(id+"F0.wireOp",EDGE,"E227.MirrorCS"),sQuery(id+"F0.wireOp",EDGE,"E228.MirrorCS")])]});
            var Q1;
            Q1=makeQuery(id+"F1.opExtrude","CAP_VERTEX",VERTEX,{"disambiguationData":[OSD([sQuery(id+"F0.wireOp",EDGE,"E102"),sQuery(id+"F0.wireOp",EDGE,"E162.MirrorCS")])],"isStart":false});
            var Q2;
            Q2=makeQuery(id+"F1.opExtrude","CAP_VERTEX",VERTEX,{"disambiguationData":[OSD([sQuery(id+"F0.wireOp",EDGE,"E102"),sQuery(id+"F0.wireOp",EDGE,"E162.MirrorCS")])],"isStart":false});
            transform(context, id + "F2", {"entities" : qUnion([Q0]), "transformType" : TransformType.SCALE_UNIFORMLY, "scale" : 1.2, "scalePoint" : qUnion([Q2]), "makeCopy" : false});
        }
        {
            var Q0;
            Q0=makeQuery(id+"F1.opExtrude","CAP_FACE",FACE,{"disambiguationData":[OSD([sQuery(id+"F0.wireOp",EDGE,"E1"),sQuery(id+"F0.wireOp",EDGE,"E2"),sQuery(id+"F0.wireOp",EDGE,"E3"),sQuery(id+"F0.wireOp",EDGE,"E4"),sQuery(id+"F0.wireOp",EDGE,"E5"),sQuery(id+"F0.wireOp",EDGE,"E6"),sQuery(id+"F0.wireOp",EDGE,"E7"),sQuery(id+"F0.wireOp",EDGE,"E8"),sQuery(id+"F0.wireOp",EDGE,"E9"),sQuery(id+"F0.wireOp",EDGE,"E10"),sQuery(id+"F0.wireOp",EDGE,"E11"),sQuery(id+"F0.wireOp",EDGE,"E12"),sQuery(id+"F0.wireOp",EDGE,"E13"),sQuery(id+"F0.wireOp",EDGE,"E14"),sQuery(id+"F0.wireOp",EDGE,"E15"),sQuery(id+"F0.wireOp",EDGE,"E16"),sQuery(id+"F0.wireOp",EDGE,"E17"),sQuery(id+"F0.wireOp",EDGE,"E18"),sQuery(id+"F0.wireOp",EDGE,"E19"),sQuery(id+"F0.wireOp",EDGE,"E20"),sQuery(id+"F0.wireOp",EDGE,"E21"),sQuery(id+"F0.wireOp",EDGE,"E22"),sQuery(id+"F0.wireOp",EDGE,"E23"),sQuery(id+"F0.wireOp",EDGE,"E24"),sQuery(id+"F0.wireOp",EDGE,"E25"),sQuery(id+"F0.wireOp",EDGE,"E26"),sQuery(id+"F0.wireOp",EDGE,"E27"),sQuery(id+"F0.wireOp",EDGE,"E28"),sQuery(id+"F0.wireOp",EDGE,"E29"),sQuery(id+"F0.wireOp",EDGE,"E30"),sQuery(id+"F0.wireOp",EDGE,"E31"),sQuery(id+"F0.wireOp",EDGE,"E32"),sQuery(id+"F0.wireOp",EDGE,"E33"),sQuery(id+"F0.wireOp",EDGE,"E34"),sQuery(id+"F0.wireOp",EDGE,"E35"),sQuery(id+"F0.wireOp",EDGE,"E36"),sQuery(id+"F0.wireOp",EDGE,"E37"),sQuery(id+"F0.wireOp",EDGE,"E38"),sQuery(id+"F0.wireOp",EDGE,"E39"),sQuery(id+"F0.wireOp",EDGE,"E40"),sQuery(id+"F0.wireOp",EDGE,"E41"),sQuery(id+"F0.wireOp",EDGE,"E42"),sQuery(id+"F0.wireOp",EDGE,"E43"),sQuery(id+"F0.wireOp",EDGE,"E44"),sQuery(id+"F0.wireOp",EDGE,"E45"),sQuery(id+"F0.wireOp",EDGE,"E46"),sQuery(id+"F0.wireOp",EDGE,"E47"),sQuery(id+"F0.wireOp",EDGE,"E48"),sQuery(id+"F0.wireOp",EDGE,"E49"),sQuery(id+"F0.wireOp",EDGE,"E50"),sQuery(id+"F0.wireOp",EDGE,"E51"),sQuery(id+"F0.wireOp",EDGE,"E52"),sQuery(id+"F0.wireOp",EDGE,"E53"),sQuery(id+"F0.wireOp",EDGE,"E54"),sQuery(id+"F0.wireOp",EDGE,"E55"),sQuery(id+"F0.wireOp",EDGE,"E56"),sQuery(id+"F0.wireOp",EDGE,"E57"),sQuery(id+"F0.wireOp",EDGE,"E58"),sQuery(id+"F0.wireOp",EDGE,"E59"),sQuery(id+"F0.wireOp",EDGE,"E60"),sQuery(id+"F0.wireOp",EDGE,"E61"),sQuery(id+"F0.wireOp",EDGE,"E62"),sQuery(id+"F0.wireOp",EDGE,"E63"),sQuery(id+"F0.wireOp",EDGE,"E64"),sQuery(id+"F0.wireOp",EDGE,"E65"),sQuery(id+"F0.wireOp",EDGE,"E66"),sQuery(id+"F0.wireOp",EDGE,"E67"),sQuery(id+"F0.wireOp",EDGE,"E68"),sQuery(id+"F0.wireOp",EDGE,"E69"),sQuery(id+"F0.wireOp",EDGE,"E70"),sQuery(id+"F0.wireOp",EDGE,"E71"),sQuery(id+"F0.wireOp",EDGE,"E72"),sQuery(id+"F0.wireOp",EDGE,"E73"),sQuery(id+"F0.wireOp",EDGE,"E74"),sQuery(id+"F0.wireOp",EDGE,"E75"),sQuery(id+"F0.wireOp",EDGE,"E76"),sQuery(id+"F0.wireOp",EDGE,"E77"),sQuery(id+"F0.wireOp",EDGE,"E78"),sQuery(id+"F0.wireOp",EDGE,"E79"),sQuery(id+"F0.wireOp",EDGE,"E80"),sQuery(id+"F0.wireOp",EDGE,"E81"),sQuery(id+"F0.wireOp",EDGE,"E82"),sQuery(id+"F0.wireOp",EDGE,"E83"),sQuery(id+"F0.wireOp",EDGE,"E84"),sQuery(id+"F0.wireOp",EDGE,"E85"),sQuery(id+"F0.wireOp",EDGE,"E86"),sQuery(id+"F0.wireOp",EDGE,"E87"),sQuery(id+"F0.wireOp",EDGE,"E88"),sQuery(id+"F0.wireOp",EDGE,"E89"),sQuery(id+"F0.wireOp",EDGE,"E90"),sQuery(id+"F0.wireOp",EDGE,"E91"),sQuery(id+"F0.wireOp",EDGE,"E92"),sQuery(id+"F0.wireOp",EDGE,"E93"),sQuery(id+"F0.wireOp",EDGE,"E94"),sQuery(id+"F0.wireOp",EDGE,"E95"),sQuery(id+"F0.wireOp",EDGE,"E96"),sQuery(id+"F0.wireOp",EDGE,"E97"),sQuery(id+"F0.wireOp",EDGE,"E98"),sQuery(id+"F0.wireOp",EDGE,"E99"),sQuery(id+"F0.wireOp",EDGE,"E100"),sQuery(id+"F0.wireOp",EDGE,"E101"),sQuery(id+"F0.wireOp",EDGE,"E102"),sQuery(id+"F0.wireOp",EDGE,"E103"),sQuery(id+"F0.wireOp",EDGE,"E104"),sQuery(id+"F0.wireOp",EDGE,"E105"),sQuery(id+"F0.wireOp",EDGE,"E106"),sQuery(id+"F0.wireOp",EDGE,"E107"),sQuery(id+"F0.wireOp",EDGE,"E108"),sQuery(id+"F0.wireOp",EDGE,"E109"),sQuery(id+"F0.wireOp",EDGE,"E110"),sQuery(id+"F0.wireOp",EDGE,"E111"),sQuery(id+"F0.wireOp",EDGE,"E112"),sQuery(id+"F0.wireOp",EDGE,"E113"),sQuery(id+"F0.wireOp",EDGE,"E114"),sQuery(id+"F0.wireOp",EDGE,"E115.MirrorCS"),sQuery(id+"F0.wireOp",EDGE,"E116.MirrorCS"),sQuery(id+"F0.wireOp",EDGE,"E117.MirrorCS"),sQuery(id+"F0.wireOp",EDGE,"E118.MirrorCS"),sQuery(id+"F0.wireOp",EDGE,"E119.MirrorCS"),sQuery(id+"F0.wireOp",EDGE,"E120.MirrorCS"),sQuery(id+"F0.wireOp",EDGE,"E121.MirrorCS"),sQuery(id+"F0.wireOp",EDGE,"E122.MirrorCS"),sQuery(id+"F0.wireOp",EDGE,"E123.MirrorCS"),sQuery(id+"F0.wireOp",EDGE,"E124.MirrorCS"),sQuery(id+"F0.wireOp",EDGE,"E125.MirrorCS"),sQuery(id+"F0.wireOp",EDGE,"E126.MirrorCS"),sQuery(id+"F0.wireOp",EDGE,"E127.MirrorCS"),sQuery(id+"F0.wireOp",EDGE,"E128.MirrorCS"),sQuery(id+"F0.wireOp",EDGE,"E129.MirrorCS"),sQuery(id+"F0.wireOp",EDGE,"E130.MirrorCS"),sQuery(id+"F0.wireOp",EDGE,"E131.MirrorCS"),sQuery(id+"F0.wireOp",EDGE,"E132.MirrorCS"),sQuery(id+"F0.wireOp",EDGE,"E133.MirrorCS"),sQuery(id+"F0.wireOp",EDGE,"E134.MirrorCS"),sQuery(id+"F0.wireOp",EDGE,"E135.MirrorCS"),sQuery(id+"F0.wireOp",EDGE,"E136.MirrorCS"),sQuery(id+"F0.wireOp",EDGE,"E137.MirrorCS"),sQuery(id+"F0.wireOp",EDGE,"E138.MirrorCS"),sQuery(id+"F0.wireOp",EDGE,"E139.MirrorCS"),sQuery(id+"F0.wireOp",EDGE,"E140.MirrorCS"),sQuery(id+"F0.wireOp",EDGE,"E141.MirrorCS"),sQuery(id+"F0.wireOp",EDGE,"E142.MirrorCS"),sQuery(id+"F0.wireOp",EDGE,"E143.MirrorCS"),sQuery(id+"F0.wireOp",EDGE,"E144.MirrorCS"),sQuery(id+"F0.wireOp",EDGE,"E145.MirrorCS"),sQuery(id+"F0.wireOp",EDGE,"E146.MirrorCS"),sQuery(id+"F0.wireOp",EDGE,"E147.MirrorCS"),sQuery(id+"F0.wireOp",EDGE,"E148.MirrorCS"),sQuery(id+"F0.wireOp",EDGE,"E149.MirrorCS"),sQuery(id+"F0.wireOp",EDGE,"E150.MirrorCS"),sQuery(id+"F0.wireOp",EDGE,"E151.MirrorCS"),sQuery(id+"F0.wireOp",EDGE,"E152.MirrorCS"),sQuery(id+"F0.wireOp",EDGE,"E153.MirrorCS"),sQuery(id+"F0.wireOp",EDGE,"E154.MirrorCS"),sQuery(id+"F0.wireOp",EDGE,"E155.MirrorCS"),sQuery(id+"F0.wireOp",EDGE,"E156.MirrorCS"),sQuery(id+"F0.wireOp",EDGE,"E157.MirrorCS"),sQuery(id+"F0.wireOp",EDGE,"E158.MirrorCS"),sQuery(id+"F0.wireOp",EDGE,"E159.MirrorCS"),sQuery(id+"F0.wireOp",EDGE,"E160.MirrorCS"),sQuery(id+"F0.wireOp",EDGE,"E161.MirrorCS"),sQuery(id+"F0.wireOp",EDGE,"E162.MirrorCS"),sQuery(id+"F0.wireOp",EDGE,"E163.MirrorCS"),sQuery(id+"F0.wireOp",EDGE,"E164.MirrorCS"),sQuery(id+"F0.wireOp",EDGE,"E165.MirrorCS"),sQuery(id+"F0.wireOp",EDGE,"E166.MirrorCS"),sQuery(id+"F0.wireOp",EDGE,"E167.MirrorCS"),sQuery(id+"F0.wireOp",EDGE,"E168.MirrorCS"),sQuery(id+"F0.wireOp",EDGE,"E169.MirrorCS"),sQuery(id+"F0.wireOp",EDGE,"E170.MirrorCS"),sQuery(id+"F0.wireOp",EDGE,"E171.MirrorCS"),sQuery(id+"F0.wireOp",EDGE,"E172.MirrorCS"),sQuery(id+"F0.wireOp",EDGE,"E173.MirrorCS"),sQuery(id+"F0.wireOp",EDGE,"E174.MirrorCS"),sQuery(id+"F0.wireOp",EDGE,"E175.MirrorCS"),sQuery(id+"F0.wireOp",EDGE,"E176.MirrorCS"),sQuery(id+"F0.wireOp",EDGE,"E177.MirrorCS"),sQuery(id+"F0.wireOp",EDGE,"E178.MirrorCS"),sQuery(id+"F0.wireOp",EDGE,"E179.MirrorCS"),sQuery(id+"F0.wireOp",EDGE,"E180.MirrorCS"),sQuery(id+"F0.wireOp",EDGE,"E181.MirrorCS"),sQuery(id+"F0.wireOp",EDGE,"E182.MirrorCS"),sQuery(id+"F0.wireOp",EDGE,"E183.MirrorCS"),sQuery(id+"F0.wireOp",EDGE,"E184.MirrorCS"),sQuery(id+"F0.wireOp",EDGE,"E185.MirrorCS"),sQuery(id+"F0.wireOp",EDGE,"E186.MirrorCS"),sQuery(id+"F0.wireOp",EDGE,"E187.MirrorCS"),sQuery(id+"F0.wireOp",EDGE,"E188.MirrorCS"),sQuery(id+"F0.wireOp",EDGE,"E189.MirrorCS"),sQuery(id+"F0.wireOp",EDGE,"E190.MirrorCS"),sQuery(id+"F0.wireOp",EDGE,"E191.MirrorCS"),sQuery(id+"F0.wireOp",EDGE,"E192.MirrorCS"),sQuery(id+"F0.wireOp",EDGE,"E193.MirrorCS"),sQuery(id+"F0.wireOp",EDGE,"E194.MirrorCS"),sQuery(id+"F0.wireOp",EDGE,"E195.MirrorCS"),sQuery(id+"F0.wireOp",EDGE,"E196.MirrorCS"),sQuery(id+"F0.wireOp",EDGE,"E197.MirrorCS"),sQuery(id+"F0.wireOp",EDGE,"E198.MirrorCS"),sQuery(id+"F0.wireOp",EDGE,"E199.MirrorCS"),sQuery(id+"F0.wireOp",EDGE,"E200.MirrorCS"),sQuery(id+"F0.wireOp",EDGE,"E201.MirrorCS"),sQuery(id+"F0.wireOp",EDGE,"E202.MirrorCS"),sQuery(id+"F0.wireOp",EDGE,"E203.MirrorCS"),sQuery(id+"F0.wireOp",EDGE,"E204.MirrorCS"),sQuery(id+"F0.wireOp",EDGE,"E205.MirrorCS"),sQuery(id+"F0.wireOp",EDGE,"E206.MirrorCS"),sQuery(id+"F0.wireOp",EDGE,"E207.MirrorCS"),sQuery(id+"F0.wireOp",EDGE,"E208.MirrorCS"),sQuery(id+"F0.wireOp",EDGE,"E209.MirrorCS"),sQuery(id+"F0.wireOp",EDGE,"E210.MirrorCS"),sQuery(id+"F0.wireOp",EDGE,"E211.MirrorCS"),sQuery(id+"F0.wireOp",EDGE,"E212.MirrorCS"),sQuery(id+"F0.wireOp",EDGE,"E213.MirrorCS"),sQuery(id+"F0.wireOp",EDGE,"E214.MirrorCS"),sQuery(id+"F0.wireOp",EDGE,"E215.MirrorCS"),sQuery(id+"F0.wireOp",EDGE,"E216.MirrorCS"),sQuery(id+"F0.wireOp",EDGE,"E217.MirrorCS"),sQuery(id+"F0.wireOp",EDGE,"E218.MirrorCS"),sQuery(id+"F0.wireOp",EDGE,"E219.MirrorCS"),sQuery(id+"F0.wireOp",EDGE,"E220.MirrorCS"),sQuery(id+"F0.wireOp",EDGE,"E221.MirrorCS"),sQuery(id+"F0.wireOp",EDGE,"E222.MirrorCS"),sQuery(id+"F0.wireOp",EDGE,"E223.MirrorCS"),sQuery(id+"F0.wireOp",EDGE,"E224.MirrorCS"),sQuery(id+"F0.wireOp",EDGE,"E225.MirrorCS"),sQuery(id+"F0.wireOp",EDGE,"E226.MirrorCS"),sQuery(id+"F0.wireOp",EDGE,"E227.MirrorCS"),sQuery(id+"F0.wireOp",EDGE,"E228.MirrorCS")])],"isStart":false});
            var sketch = newSketch(context, id + "F3", { "sketchPlane" : qUnion([Q0])});
            skLineSegment(sketch, "E229.bottom", {"start": v(3.83, -14.17) * mm, "end": v(20.83, -14.17) * mm});
            skLineSegment(sketch, "E229.top", {"start": v(3.83, -40.17) * mm, "end": v(20.83, -40.17) * mm});
            skLineSegment(sketch, "E229.left", {"start": v(3.83, -14.17) * mm, "end": v(3.83, -40.17) * mm});
            skLineSegment(sketch, "E229.right", {"start": v(20.83, -14.17) * mm, "end": v(20.83, -40.17) * mm});
            skLineSegment(sketch, "E230", {"start": v(3.83, -40.17) * mm, "end": v(-48.3, -40.17) * mm});
            skLineSegment(sketch, "E231", {"start": v(-48.3, -40.17) * mm, "end": v(-58.3, -45.95) * mm});
            skLineSegment(sketch, "E232", {"start": v(-58.3, -45.95) * mm, "end": v(-58.3, -58.17) * mm});
            skLineSegment(sketch, "E233", {"start": v(-58.3, -58.17) * mm, "end": v(84.96, -58.17) * mm});
            skLineSegment(sketch, "E234", {"start": v(84.96, -58.17) * mm, "end": v(84.96, -45.95) * mm});
            skLineSegment(sketch, "E235", {"start": v(84.96, -45.95) * mm, "end": v(74.96, -40.17) * mm});
            skLineSegment(sketch, "E236", {"start": v(74.96, -40.17) * mm, "end": v(20.83, -40.17) * mm});
            skLineSegment(sketch, "E237", {"start": v(-61.67, 0) * mm, "end": v(88.33, 0) * mm, "construction": true});
            skLineSegment(sketch, "E238", {"start": v(13.33, 0) * mm, "end": v(13.33, -40.17) * mm, "construction": true});
            skText(sketch, "E239", { "text": "SSV NORMANDY", "fontName": "OpenSans-Bold.ttf"});
            skLineSegment(sketch, "E240", {"start": v(-48.3, -58.17) * mm, "end": v(-28.1, -93.17) * mm});
            skLineSegment(sketch, "E241", {"start": v(-28.1, -93.17) * mm, "end": v(54.76, -93.17) * mm});
            skLineSegment(sketch, "E242", {"start": v(54.76, -93.17) * mm, "end": v(74.96, -58.17) * mm});
            skLineSegment(sketch, "E243.0", {"start": v(48.98, -83.17) * mm, "end": v(63.42, -58.17) * mm});
            skLineSegment(sketch, "E243.1", {"start": v(-22.32, -83.17) * mm, "end": v(48.98, -83.17) * mm});
            skLineSegment(sketch, "E243.2", {"start": v(-36.76, -58.17) * mm, "end": v(-22.32, -83.17) * mm});
            const initialGuessF3  = {"E239": [-0.0433, -0.05417, 1, 0, 0.01]};
            skSetInitialGuess(sketch, initialGuessF3);
            skSolve(sketch);
        }
        {
            var Q0;
            Q0=makeQuery(id+"F3.imprint","IMPRINT",FACE,{"disambiguationData":[TD([[makeQuery(id+"F3.imprint","IMPRINT",EDGE,{"derivedFrom":sQuery(id+"F3.wireOp",EDGE,"E239.sketch_text.stroke-165")}),1.0]])]});
            var Q1;
            Q1=makeQuery(id+"F3.imprint","IMPRINT",FACE,{"disambiguationData":[TD([[makeQuery(id+"F3.imprint","IMPRINT",EDGE,{"derivedFrom":sQuery(id+"F3.wireOp",EDGE,"E229.top")}),-1.0]])]});
            var Q2;
            {var subQ0=sQuery(id+"F3.wireOp",EDGE,"E240");Q2=makeQuery(id+"F3.imprint","IMPRINT",FACE,{"disambiguationData":[TD([[makeQuery(id+"F3.imprint","IMPRINT",EDGE,{"derivedFrom":subQ0}),1.0]])]});}
            var Q3;
            {var subQ1=sQuery(id+"F3.wireOp",EDGE,"E229.top");Q3=makeQuery(id+"F3.imprint","IMPRINT",FACE,{"disambiguationData":[TD([[makeQuery(id+"F3.imprint","IMPRINT",EDGE,{"derivedFrom":subQ1}),1.0]])]});}
            var Q4;
            Q4=makeQuery(id+"F3.imprint","IMPRINT",FACE,{"disambiguationData":[TD([[makeQuery(id+"F3.imprint","IMPRINT",EDGE,{"derivedFrom":sQuery(id+"F3.wireOp",EDGE,"E239.sketch_text.stroke-88")}),1.0]])]});
            var Q5;
            Q5=makeQuery(id+"F3.imprint","IMPRINT",FACE,{"disambiguationData":[TD([[makeQuery(id+"F3.imprint","IMPRINT",EDGE,{"derivedFrom":sQuery(id+"F3.wireOp",EDGE,"E239.sketch_text.stroke-94")}),1.0]])]});
            var Q6;
            Q6=makeQuery(id+"F3.imprint","IMPRINT",FACE,{"disambiguationData":[TD([[makeQuery(id+"F3.imprint","IMPRINT",EDGE,{"derivedFrom":sQuery(id+"F3.wireOp",EDGE,"E239.sketch_text.stroke-140")}),1.0]])]});
            var Q7;
            Q7=makeQuery(id+"F1.opExtrude","CAP_FACE",FACE,{"disambiguationData":[OSD([sQuery(id+"F0.wireOp",EDGE,"E1"),sQuery(id+"F0.wireOp",EDGE,"E2"),sQuery(id+"F0.wireOp",EDGE,"E3"),sQuery(id+"F0.wireOp",EDGE,"E4"),sQuery(id+"F0.wireOp",EDGE,"E5"),sQuery(id+"F0.wireOp",EDGE,"E6"),sQuery(id+"F0.wireOp",EDGE,"E7"),sQuery(id+"F0.wireOp",EDGE,"E8"),sQuery(id+"F0.wireOp",EDGE,"E9"),sQuery(id+"F0.wireOp",EDGE,"E10"),sQuery(id+"F0.wireOp",EDGE,"E11"),sQuery(id+"F0.wireOp",EDGE,"E12"),sQuery(id+"F0.wireOp",EDGE,"E13"),sQuery(id+"F0.wireOp",EDGE,"E14"),sQuery(id+"F0.wireOp",EDGE,"E15"),sQuery(id+"F0.wireOp",EDGE,"E16"),sQuery(id+"F0.wireOp",EDGE,"E17"),sQuery(id+"F0.wireOp",EDGE,"E18"),sQuery(id+"F0.wireOp",EDGE,"E19"),sQuery(id+"F0.wireOp",EDGE,"E20"),sQuery(id+"F0.wireOp",EDGE,"E21"),sQuery(id+"F0.wireOp",EDGE,"E22"),sQuery(id+"F0.wireOp",EDGE,"E23"),sQuery(id+"F0.wireOp",EDGE,"E24"),sQuery(id+"F0.wireOp",EDGE,"E25"),sQuery(id+"F0.wireOp",EDGE,"E26"),sQuery(id+"F0.wireOp",EDGE,"E27"),sQuery(id+"F0.wireOp",EDGE,"E28"),sQuery(id+"F0.wireOp",EDGE,"E29"),sQuery(id+"F0.wireOp",EDGE,"E30"),sQuery(id+"F0.wireOp",EDGE,"E31"),sQuery(id+"F0.wireOp",EDGE,"E32"),sQuery(id+"F0.wireOp",EDGE,"E33"),sQuery(id+"F0.wireOp",EDGE,"E34"),sQuery(id+"F0.wireOp",EDGE,"E35"),sQuery(id+"F0.wireOp",EDGE,"E36"),sQuery(id+"F0.wireOp",EDGE,"E37"),sQuery(id+"F0.wireOp",EDGE,"E38"),sQuery(id+"F0.wireOp",EDGE,"E39"),sQuery(id+"F0.wireOp",EDGE,"E40"),sQuery(id+"F0.wireOp",EDGE,"E41"),sQuery(id+"F0.wireOp",EDGE,"E42"),sQuery(id+"F0.wireOp",EDGE,"E43"),sQuery(id+"F0.wireOp",EDGE,"E44"),sQuery(id+"F0.wireOp",EDGE,"E45"),sQuery(id+"F0.wireOp",EDGE,"E46"),sQuery(id+"F0.wireOp",EDGE,"E47"),sQuery(id+"F0.wireOp",EDGE,"E48"),sQuery(id+"F0.wireOp",EDGE,"E49"),sQuery(id+"F0.wireOp",EDGE,"E50"),sQuery(id+"F0.wireOp",EDGE,"E51"),sQuery(id+"F0.wireOp",EDGE,"E52"),sQuery(id+"F0.wireOp",EDGE,"E53"),sQuery(id+"F0.wireOp",EDGE,"E54"),sQuery(id+"F0.wireOp",EDGE,"E55"),sQuery(id+"F0.wireOp",EDGE,"E56"),sQuery(id+"F0.wireOp",EDGE,"E57"),sQuery(id+"F0.wireOp",EDGE,"E58"),sQuery(id+"F0.wireOp",EDGE,"E59"),sQuery(id+"F0.wireOp",EDGE,"E60"),sQuery(id+"F0.wireOp",EDGE,"E61"),sQuery(id+"F0.wireOp",EDGE,"E62"),sQuery(id+"F0.wireOp",EDGE,"E63"),sQuery(id+"F0.wireOp",EDGE,"E64"),sQuery(id+"F0.wireOp",EDGE,"E65"),sQuery(id+"F0.wireOp",EDGE,"E66"),sQuery(id+"F0.wireOp",EDGE,"E67"),sQuery(id+"F0.wireOp",EDGE,"E68"),sQuery(id+"F0.wireOp",EDGE,"E69"),sQuery(id+"F0.wireOp",EDGE,"E70"),sQuery(id+"F0.wireOp",EDGE,"E71"),sQuery(id+"F0.wireOp",EDGE,"E72"),sQuery(id+"F0.wireOp",EDGE,"E73"),sQuery(id+"F0.wireOp",EDGE,"E74"),sQuery(id+"F0.wireOp",EDGE,"E75"),sQuery(id+"F0.wireOp",EDGE,"E76"),sQuery(id+"F0.wireOp",EDGE,"E77"),sQuery(id+"F0.wireOp",EDGE,"E78"),sQuery(id+"F0.wireOp",EDGE,"E79"),sQuery(id+"F0.wireOp",EDGE,"E80"),sQuery(id+"F0.wireOp",EDGE,"E81"),sQuery(id+"F0.wireOp",EDGE,"E82"),sQuery(id+"F0.wireOp",EDGE,"E83"),sQuery(id+"F0.wireOp",EDGE,"E84"),sQuery(id+"F0.wireOp",EDGE,"E85"),sQuery(id+"F0.wireOp",EDGE,"E86"),sQuery(id+"F0.wireOp",EDGE,"E87"),sQuery(id+"F0.wireOp",EDGE,"E88"),sQuery(id+"F0.wireOp",EDGE,"E89"),sQuery(id+"F0.wireOp",EDGE,"E90"),sQuery(id+"F0.wireOp",EDGE,"E91"),sQuery(id+"F0.wireOp",EDGE,"E92"),sQuery(id+"F0.wireOp",EDGE,"E93"),sQuery(id+"F0.wireOp",EDGE,"E94"),sQuery(id+"F0.wireOp",EDGE,"E95"),sQuery(id+"F0.wireOp",EDGE,"E96"),sQuery(id+"F0.wireOp",EDGE,"E97"),sQuery(id+"F0.wireOp",EDGE,"E98"),sQuery(id+"F0.wireOp",EDGE,"E99"),sQuery(id+"F0.wireOp",EDGE,"E100"),sQuery(id+"F0.wireOp",EDGE,"E101"),sQuery(id+"F0.wireOp",EDGE,"E102"),sQuery(id+"F0.wireOp",EDGE,"E103"),sQuery(id+"F0.wireOp",EDGE,"E104"),sQuery(id+"F0.wireOp",EDGE,"E105"),sQuery(id+"F0.wireOp",EDGE,"E106"),sQuery(id+"F0.wireOp",EDGE,"E107"),sQuery(id+"F0.wireOp",EDGE,"E108"),sQuery(id+"F0.wireOp",EDGE,"E109"),sQuery(id+"F0.wireOp",EDGE,"E110"),sQuery(id+"F0.wireOp",EDGE,"E111"),sQuery(id+"F0.wireOp",EDGE,"E112"),sQuery(id+"F0.wireOp",EDGE,"E113"),sQuery(id+"F0.wireOp",EDGE,"E114"),sQuery(id+"F0.wireOp",EDGE,"E115.MirrorCS"),sQuery(id+"F0.wireOp",EDGE,"E116.MirrorCS"),sQuery(id+"F0.wireOp",EDGE,"E117.MirrorCS"),sQuery(id+"F0.wireOp",EDGE,"E118.MirrorCS"),sQuery(id+"F0.wireOp",EDGE,"E119.MirrorCS"),sQuery(id+"F0.wireOp",EDGE,"E120.MirrorCS"),sQuery(id+"F0.wireOp",EDGE,"E121.MirrorCS"),sQuery(id+"F0.wireOp",EDGE,"E122.MirrorCS"),sQuery(id+"F0.wireOp",EDGE,"E123.MirrorCS"),sQuery(id+"F0.wireOp",EDGE,"E124.MirrorCS"),sQuery(id+"F0.wireOp",EDGE,"E125.MirrorCS"),sQuery(id+"F0.wireOp",EDGE,"E126.MirrorCS"),sQuery(id+"F0.wireOp",EDGE,"E127.MirrorCS"),sQuery(id+"F0.wireOp",EDGE,"E128.MirrorCS"),sQuery(id+"F0.wireOp",EDGE,"E129.MirrorCS"),sQuery(id+"F0.wireOp",EDGE,"E130.MirrorCS"),sQuery(id+"F0.wireOp",EDGE,"E131.MirrorCS"),sQuery(id+"F0.wireOp",EDGE,"E132.MirrorCS"),sQuery(id+"F0.wireOp",EDGE,"E133.MirrorCS"),sQuery(id+"F0.wireOp",EDGE,"E134.MirrorCS"),sQuery(id+"F0.wireOp",EDGE,"E135.MirrorCS"),sQuery(id+"F0.wireOp",EDGE,"E136.MirrorCS"),sQuery(id+"F0.wireOp",EDGE,"E137.MirrorCS"),sQuery(id+"F0.wireOp",EDGE,"E138.MirrorCS"),sQuery(id+"F0.wireOp",EDGE,"E139.MirrorCS"),sQuery(id+"F0.wireOp",EDGE,"E140.MirrorCS"),sQuery(id+"F0.wireOp",EDGE,"E141.MirrorCS"),sQuery(id+"F0.wireOp",EDGE,"E142.MirrorCS"),sQuery(id+"F0.wireOp",EDGE,"E143.MirrorCS"),sQuery(id+"F0.wireOp",EDGE,"E144.MirrorCS"),sQuery(id+"F0.wireOp",EDGE,"E145.MirrorCS"),sQuery(id+"F0.wireOp",EDGE,"E146.MirrorCS"),sQuery(id+"F0.wireOp",EDGE,"E147.MirrorCS"),sQuery(id+"F0.wireOp",EDGE,"E148.MirrorCS"),sQuery(id+"F0.wireOp",EDGE,"E149.MirrorCS"),sQuery(id+"F0.wireOp",EDGE,"E150.MirrorCS"),sQuery(id+"F0.wireOp",EDGE,"E151.MirrorCS"),sQuery(id+"F0.wireOp",EDGE,"E152.MirrorCS"),sQuery(id+"F0.wireOp",EDGE,"E153.MirrorCS"),sQuery(id+"F0.wireOp",EDGE,"E154.MirrorCS"),sQuery(id+"F0.wireOp",EDGE,"E155.MirrorCS"),sQuery(id+"F0.wireOp",EDGE,"E156.MirrorCS"),sQuery(id+"F0.wireOp",EDGE,"E157.MirrorCS"),sQuery(id+"F0.wireOp",EDGE,"E158.MirrorCS"),sQuery(id+"F0.wireOp",EDGE,"E159.MirrorCS"),sQuery(id+"F0.wireOp",EDGE,"E160.MirrorCS"),sQuery(id+"F0.wireOp",EDGE,"E161.MirrorCS"),sQuery(id+"F0.wireOp",EDGE,"E162.MirrorCS"),sQuery(id+"F0.wireOp",EDGE,"E163.MirrorCS"),sQuery(id+"F0.wireOp",EDGE,"E164.MirrorCS"),sQuery(id+"F0.wireOp",EDGE,"E165.MirrorCS"),sQuery(id+"F0.wireOp",EDGE,"E166.MirrorCS"),sQuery(id+"F0.wireOp",EDGE,"E167.MirrorCS"),sQuery(id+"F0.wireOp",EDGE,"E168.MirrorCS"),sQuery(id+"F0.wireOp",EDGE,"E169.MirrorCS"),sQuery(id+"F0.wireOp",EDGE,"E170.MirrorCS"),sQuery(id+"F0.wireOp",EDGE,"E171.MirrorCS"),sQuery(id+"F0.wireOp",EDGE,"E172.MirrorCS"),sQuery(id+"F0.wireOp",EDGE,"E173.MirrorCS"),sQuery(id+"F0.wireOp",EDGE,"E174.MirrorCS"),sQuery(id+"F0.wireOp",EDGE,"E175.MirrorCS"),sQuery(id+"F0.wireOp",EDGE,"E176.MirrorCS"),sQuery(id+"F0.wireOp",EDGE,"E177.MirrorCS"),sQuery(id+"F0.wireOp",EDGE,"E178.MirrorCS"),sQuery(id+"F0.wireOp",EDGE,"E179.MirrorCS"),sQuery(id+"F0.wireOp",EDGE,"E180.MirrorCS"),sQuery(id+"F0.wireOp",EDGE,"E181.MirrorCS"),sQuery(id+"F0.wireOp",EDGE,"E182.MirrorCS"),sQuery(id+"F0.wireOp",EDGE,"E183.MirrorCS"),sQuery(id+"F0.wireOp",EDGE,"E184.MirrorCS"),sQuery(id+"F0.wireOp",EDGE,"E185.MirrorCS"),sQuery(id+"F0.wireOp",EDGE,"E186.MirrorCS"),sQuery(id+"F0.wireOp",EDGE,"E187.MirrorCS"),sQuery(id+"F0.wireOp",EDGE,"E188.MirrorCS"),sQuery(id+"F0.wireOp",EDGE,"E189.MirrorCS"),sQuery(id+"F0.wireOp",EDGE,"E190.MirrorCS"),sQuery(id+"F0.wireOp",EDGE,"E191.MirrorCS"),sQuery(id+"F0.wireOp",EDGE,"E192.MirrorCS"),sQuery(id+"F0.wireOp",EDGE,"E193.MirrorCS"),sQuery(id+"F0.wireOp",EDGE,"E194.MirrorCS"),sQuery(id+"F0.wireOp",EDGE,"E195.MirrorCS"),sQuery(id+"F0.wireOp",EDGE,"E196.MirrorCS"),sQuery(id+"F0.wireOp",EDGE,"E197.MirrorCS"),sQuery(id+"F0.wireOp",EDGE,"E198.MirrorCS"),sQuery(id+"F0.wireOp",EDGE,"E199.MirrorCS"),sQuery(id+"F0.wireOp",EDGE,"E200.MirrorCS"),sQuery(id+"F0.wireOp",EDGE,"E201.MirrorCS"),sQuery(id+"F0.wireOp",EDGE,"E202.MirrorCS"),sQuery(id+"F0.wireOp",EDGE,"E203.MirrorCS"),sQuery(id+"F0.wireOp",EDGE,"E204.MirrorCS"),sQuery(id+"F0.wireOp",EDGE,"E205.MirrorCS"),sQuery(id+"F0.wireOp",EDGE,"E206.MirrorCS"),sQuery(id+"F0.wireOp",EDGE,"E207.MirrorCS"),sQuery(id+"F0.wireOp",EDGE,"E208.MirrorCS"),sQuery(id+"F0.wireOp",EDGE,"E209.MirrorCS"),sQuery(id+"F0.wireOp",EDGE,"E210.MirrorCS"),sQuery(id+"F0.wireOp",EDGE,"E211.MirrorCS"),sQuery(id+"F0.wireOp",EDGE,"E212.MirrorCS"),sQuery(id+"F0.wireOp",EDGE,"E213.MirrorCS"),sQuery(id+"F0.wireOp",EDGE,"E214.MirrorCS"),sQuery(id+"F0.wireOp",EDGE,"E215.MirrorCS"),sQuery(id+"F0.wireOp",EDGE,"E216.MirrorCS"),sQuery(id+"F0.wireOp",EDGE,"E217.MirrorCS"),sQuery(id+"F0.wireOp",EDGE,"E218.MirrorCS"),sQuery(id+"F0.wireOp",EDGE,"E219.MirrorCS"),sQuery(id+"F0.wireOp",EDGE,"E220.MirrorCS"),sQuery(id+"F0.wireOp",EDGE,"E221.MirrorCS"),sQuery(id+"F0.wireOp",EDGE,"E222.MirrorCS"),sQuery(id+"F0.wireOp",EDGE,"E223.MirrorCS"),sQuery(id+"F0.wireOp",EDGE,"E224.MirrorCS"),sQuery(id+"F0.wireOp",EDGE,"E225.MirrorCS"),sQuery(id+"F0.wireOp",EDGE,"E226.MirrorCS"),sQuery(id+"F0.wireOp",EDGE,"E227.MirrorCS"),sQuery(id+"F0.wireOp",EDGE,"E228.MirrorCS")])],"isStart":true});
            extrude(context, id + "F4", {"entities" : qUnion([Q0, Q1, Q2, Q3, Q4, Q5, Q6]), "operationType" : NewBodyOperationType.ADD, "endBound" : BoundingType.UP_TO_SURFACE, "oppositeDirection" : true, "depth" : 25 * mm, "endBoundEntityFace" : qUnion([Q7]), "offsetDistance" : 25 * mm});
        }
        {
            var Q0;
            Q0=makeQuery(id+"F4.opExtrude","SWEPT_EDGE",EDGE,{"disambiguationData":[OSD([sQuery(id+"F3.wireOp",EDGE,"E230"),sQuery(id+"F3.wireOp",EDGE,"E231")])]});
            var Q1;
            Q1=makeQuery(id+"F4.opExtrude","SWEPT_EDGE",EDGE,{"disambiguationData":[OSD([sQuery(id+"F3.wireOp",EDGE,"E231"),sQuery(id+"F3.wireOp",EDGE,"E232")])]});
            var Q2;
            Q2=makeQuery(id+"F4.opExtrude","SWEPT_EDGE",EDGE,{"disambiguationData":[OSD([sQuery(id+"F3.wireOp",EDGE,"E232"),sQuery(id+"F3.wireOp",EDGE,"E233")])]});
            var Q3;
            Q3=makeQuery(id+"F4.opExtrude","SWEPT_EDGE",EDGE,{"disambiguationData":[OSD([sQuery(id+"F3.wireOp",EDGE,"E235"),sQuery(id+"F3.wireOp",EDGE,"E236")])]});
            var Q4;
            Q4=makeQuery(id+"F4.opExtrude","SWEPT_EDGE",EDGE,{"disambiguationData":[OSD([sQuery(id+"F3.wireOp",EDGE,"E234"),sQuery(id+"F3.wireOp",EDGE,"E235")])]});
            var Q5;
            Q5=makeQuery(id+"F4.opExtrude","SWEPT_EDGE",EDGE,{"disambiguationData":[OSD([sQuery(id+"F3.wireOp",EDGE,"E233"),sQuery(id+"F3.wireOp",EDGE,"E234")])]});
            var Q6;
            Q6=makeQuery(id+"F4.opExtrude","SWEPT_EDGE",EDGE,{"disambiguationData":[OSD([sQuery(id+"F3.wireOp",EDGE,"E243.0"),sQuery(id+"F3.wireOp",EDGE,"E243.1")])]});
            var Q7;
            Q7=makeQuery(id+"F4.opExtrude","SWEPT_EDGE",EDGE,{"disambiguationData":[OSD([sQuery(id+"F3.wireOp",EDGE,"E243.1"),sQuery(id+"F3.wireOp",EDGE,"E243.2")])]});
            fillet(context, id + "F5", {"entities" : qUnion([Q0, Q1, Q2, Q3, Q4, Q5, Q6, Q7]), "radius" : 5 * mm, "tangentPropagation" : true, "allowEdgeOverflow" : false});
        }
        {
            var Q0;
            Q0=makeQuery(id+"F4.opExtrude","SWEPT_EDGE",EDGE,{"disambiguationData":[OSD([sQuery(id+"F3.wireOp",EDGE,"E240"),sQuery(id+"F3.wireOp",EDGE,"E241")])]});
            var Q1;
            Q1=makeQuery(id+"F4.opExtrude","SWEPT_EDGE",EDGE,{"disambiguationData":[OSD([sQuery(id+"F3.wireOp",EDGE,"E241"),sQuery(id+"F3.wireOp",EDGE,"E242")])]});
            fillet(context, id + "F6", {"entities" : qUnion([Q0, Q1]), "radius" : 15 * mm, "tangentPropagation" : true, "allowEdgeOverflow" : false});
        }
        {
            var Q0;
            {var subQ0=sQuery(id+"F0.wireOp",EDGE,"E221.MirrorCS");var subQ1=sQuery(id+"F0.wireOp",EDGE,"E211.MirrorCS");var subQ2=sQuery(id+"F0.wireOp",EDGE,"E202.MirrorCS");var subQ3=sQuery(id+"F0.wireOp",EDGE,"E173.MirrorCS");Q0=makeQuery(id+"F4.boolean.opBoolean","MERGE",FACE,{"derivedFrom":[makeQuery(id+"F1.opExtrude","CAP_FACE",FACE,{"disambiguationData":[OSD([sQuery(id+"F0.wireOp",EDGE,"E1"),sQuery(id+"F0.wireOp",EDGE,"E2"),sQuery(id+"F0.wireOp",EDGE,"E3"),sQuery(id+"F0.wireOp",EDGE,"E4"),sQuery(id+"F0.wireOp",EDGE,"E5"),sQuery(id+"F0.wireOp",EDGE,"E6"),sQuery(id+"F0.wireOp",EDGE,"E7"),sQuery(id+"F0.wireOp",EDGE,"E8"),sQuery(id+"F0.wireOp",EDGE,"E9"),sQuery(id+"F0.wireOp",EDGE,"E10"),sQuery(id+"F0.wireOp",EDGE,"E11"),sQuery(id+"F0.wireOp",EDGE,"E12"),sQuery(id+"F0.wireOp",EDGE,"E13"),sQuery(id+"F0.wireOp",EDGE,"E14"),sQuery(id+"F0.wireOp",EDGE,"E15"),sQuery(id+"F0.wireOp",EDGE,"E16"),sQuery(id+"F0.wireOp",EDGE,"E17"),sQuery(id+"F0.wireOp",EDGE,"E18"),sQuery(id+"F0.wireOp",EDGE,"E19"),sQuery(id+"F0.wireOp",EDGE,"E20"),sQuery(id+"F0.wireOp",EDGE,"E21"),sQuery(id+"F0.wireOp",EDGE,"E22"),sQuery(id+"F0.wireOp",EDGE,"E23"),sQuery(id+"F0.wireOp",EDGE,"E24"),sQuery(id+"F0.wireOp",EDGE,"E25"),sQuery(id+"F0.wireOp",EDGE,"E26"),sQuery(id+"F0.wireOp",EDGE,"E27"),sQuery(id+"F0.wireOp",EDGE,"E28"),sQuery(id+"F0.wireOp",EDGE,"E29"),sQuery(id+"F0.wireOp",EDGE,"E30"),sQuery(id+"F0.wireOp",EDGE,"E31"),sQuery(id+"F0.wireOp",EDGE,"E32"),sQuery(id+"F0.wireOp",EDGE,"E33"),sQuery(id+"F0.wireOp",EDGE,"E34"),sQuery(id+"F0.wireOp",EDGE,"E35"),sQuery(id+"F0.wireOp",EDGE,"E36"),sQuery(id+"F0.wireOp",EDGE,"E37"),sQuery(id+"F0.wireOp",EDGE,"E38"),sQuery(id+"F0.wireOp",EDGE,"E39"),sQuery(id+"F0.wireOp",EDGE,"E40"),sQuery(id+"F0.wireOp",EDGE,"E41"),sQuery(id+"F0.wireOp",EDGE,"E42"),sQuery(id+"F0.wireOp",EDGE,"E43"),sQuery(id+"F0.wireOp",EDGE,"E44"),sQuery(id+"F0.wireOp",EDGE,"E45"),sQuery(id+"F0.wireOp",EDGE,"E46"),sQuery(id+"F0.wireOp",EDGE,"E47"),sQuery(id+"F0.wireOp",EDGE,"E48"),sQuery(id+"F0.wireOp",EDGE,"E49"),sQuery(id+"F0.wireOp",EDGE,"E50"),sQuery(id+"F0.wireOp",EDGE,"E51"),sQuery(id+"F0.wireOp",EDGE,"E52"),sQuery(id+"F0.wireOp",EDGE,"E53"),sQuery(id+"F0.wireOp",EDGE,"E54"),sQuery(id+"F0.wireOp",EDGE,"E55"),sQuery(id+"F0.wireOp",EDGE,"E56"),sQuery(id+"F0.wireOp",EDGE,"E57"),sQuery(id+"F0.wireOp",EDGE,"E58"),sQuery(id+"F0.wireOp",EDGE,"E59"),sQuery(id+"F0.wireOp",EDGE,"E60"),sQuery(id+"F0.wireOp",EDGE,"E61"),sQuery(id+"F0.wireOp",EDGE,"E62"),sQuery(id+"F0.wireOp",EDGE,"E63"),sQuery(id+"F0.wireOp",EDGE,"E64"),sQuery(id+"F0.wireOp",EDGE,"E65"),sQuery(id+"F0.wireOp",EDGE,"E66"),sQuery(id+"F0.wireOp",EDGE,"E67"),sQuery(id+"F0.wireOp",EDGE,"E68"),sQuery(id+"F0.wireOp",EDGE,"E69"),sQuery(id+"F0.wireOp",EDGE,"E70"),sQuery(id+"F0.wireOp",EDGE,"E71"),sQuery(id+"F0.wireOp",EDGE,"E72"),sQuery(id+"F0.wireOp",EDGE,"E73"),sQuery(id+"F0.wireOp",EDGE,"E74"),sQuery(id+"F0.wireOp",EDGE,"E75"),sQuery(id+"F0.wireOp",EDGE,"E76"),sQuery(id+"F0.wireOp",EDGE,"E77"),sQuery(id+"F0.wireOp",EDGE,"E78"),sQuery(id+"F0.wireOp",EDGE,"E79"),sQuery(id+"F0.wireOp",EDGE,"E80"),sQuery(id+"F0.wireOp",EDGE,"E81"),sQuery(id+"F0.wireOp",EDGE,"E82"),sQuery(id+"F0.wireOp",EDGE,"E83"),sQuery(id+"F0.wireOp",EDGE,"E84"),sQuery(id+"F0.wireOp",EDGE,"E85"),sQuery(id+"F0.wireOp",EDGE,"E86"),sQuery(id+"F0.wireOp",EDGE,"E87"),sQuery(id+"F0.wireOp",EDGE,"E88"),sQuery(id+"F0.wireOp",EDGE,"E89"),sQuery(id+"F0.wireOp",EDGE,"E90"),sQuery(id+"F0.wireOp",EDGE,"E91"),sQuery(id+"F0.wireOp",EDGE,"E92"),sQuery(id+"F0.wireOp",EDGE,"E93"),sQuery(id+"F0.wireOp",EDGE,"E94"),sQuery(id+"F0.wireOp",EDGE,"E95"),sQuery(id+"F0.wireOp",EDGE,"E96"),sQuery(id+"F0.wireOp",EDGE,"E97"),sQuery(id+"F0.wireOp",EDGE,"E98"),sQuery(id+"F0.wireOp",EDGE,"E99"),sQuery(id+"F0.wireOp",EDGE,"E100"),sQuery(id+"F0.wireOp",EDGE,"E101"),sQuery(id+"F0.wireOp",EDGE,"E102"),sQuery(id+"F0.wireOp",EDGE,"E103"),sQuery(id+"F0.wireOp",EDGE,"E104"),sQuery(id+"F0.wireOp",EDGE,"E105"),sQuery(id+"F0.wireOp",EDGE,"E106"),sQuery(id+"F0.wireOp",EDGE,"E107"),sQuery(id+"F0.wireOp",EDGE,"E108"),sQuery(id+"F0.wireOp",EDGE,"E109"),sQuery(id+"F0.wireOp",EDGE,"E110"),sQuery(id+"F0.wireOp",EDGE,"E111"),sQuery(id+"F0.wireOp",EDGE,"E112"),sQuery(id+"F0.wireOp",EDGE,"E113"),sQuery(id+"F0.wireOp",EDGE,"E114"),sQuery(id+"F0.wireOp",EDGE,"E115.MirrorCS"),sQuery(id+"F0.wireOp",EDGE,"E116.MirrorCS"),sQuery(id+"F0.wireOp",EDGE,"E117.MirrorCS"),sQuery(id+"F0.wireOp",EDGE,"E118.MirrorCS"),sQuery(id+"F0.wireOp",EDGE,"E119.MirrorCS"),sQuery(id+"F0.wireOp",EDGE,"E120.MirrorCS"),sQuery(id+"F0.wireOp",EDGE,"E121.MirrorCS"),sQuery(id+"F0.wireOp",EDGE,"E122.MirrorCS"),sQuery(id+"F0.wireOp",EDGE,"E123.MirrorCS"),sQuery(id+"F0.wireOp",EDGE,"E124.MirrorCS"),sQuery(id+"F0.wireOp",EDGE,"E125.MirrorCS"),sQuery(id+"F0.wireOp",EDGE,"E126.MirrorCS"),sQuery(id+"F0.wireOp",EDGE,"E127.MirrorCS"),sQuery(id+"F0.wireOp",EDGE,"E128.MirrorCS"),sQuery(id+"F0.wireOp",EDGE,"E129.MirrorCS"),sQuery(id+"F0.wireOp",EDGE,"E130.MirrorCS"),sQuery(id+"F0.wireOp",EDGE,"E131.MirrorCS"),sQuery(id+"F0.wireOp",EDGE,"E132.MirrorCS"),sQuery(id+"F0.wireOp",EDGE,"E133.MirrorCS"),sQuery(id+"F0.wireOp",EDGE,"E134.MirrorCS"),sQuery(id+"F0.wireOp",EDGE,"E135.MirrorCS"),sQuery(id+"F0.wireOp",EDGE,"E136.MirrorCS"),sQuery(id+"F0.wireOp",EDGE,"E137.MirrorCS"),sQuery(id+"F0.wireOp",EDGE,"E138.MirrorCS"),sQuery(id+"F0.wireOp",EDGE,"E139.MirrorCS"),sQuery(id+"F0.wireOp",EDGE,"E140.MirrorCS"),sQuery(id+"F0.wireOp",EDGE,"E141.MirrorCS"),sQuery(id+"F0.wireOp",EDGE,"E142.MirrorCS"),sQuery(id+"F0.wireOp",EDGE,"E143.MirrorCS"),sQuery(id+"F0.wireOp",EDGE,"E144.MirrorCS"),sQuery(id+"F0.wireOp",EDGE,"E145.MirrorCS"),sQuery(id+"F0.wireOp",EDGE,"E146.MirrorCS"),sQuery(id+"F0.wireOp",EDGE,"E147.MirrorCS"),sQuery(id+"F0.wireOp",EDGE,"E148.MirrorCS"),sQuery(id+"F0.wireOp",EDGE,"E149.MirrorCS"),sQuery(id+"F0.wireOp",EDGE,"E150.MirrorCS"),sQuery(id+"F0.wireOp",EDGE,"E151.MirrorCS"),sQuery(id+"F0.wireOp",EDGE,"E152.MirrorCS"),sQuery(id+"F0.wireOp",EDGE,"E153.MirrorCS"),sQuery(id+"F0.wireOp",EDGE,"E154.MirrorCS"),sQuery(id+"F0.wireOp",EDGE,"E155.MirrorCS"),sQuery(id+"F0.wireOp",EDGE,"E156.MirrorCS"),sQuery(id+"F0.wireOp",EDGE,"E157.MirrorCS"),sQuery(id+"F0.wireOp",EDGE,"E158.MirrorCS"),sQuery(id+"F0.wireOp",EDGE,"E159.MirrorCS"),sQuery(id+"F0.wireOp",EDGE,"E160.MirrorCS"),sQuery(id+"F0.wireOp",EDGE,"E161.MirrorCS"),sQuery(id+"F0.wireOp",EDGE,"E162.MirrorCS"),sQuery(id+"F0.wireOp",EDGE,"E163.MirrorCS"),sQuery(id+"F0.wireOp",EDGE,"E164.MirrorCS"),sQuery(id+"F0.wireOp",EDGE,"E165.MirrorCS"),sQuery(id+"F0.wireOp",EDGE,"E166.MirrorCS"),sQuery(id+"F0.wireOp",EDGE,"E167.MirrorCS"),sQuery(id+"F0.wireOp",EDGE,"E168.MirrorCS"),sQuery(id+"F0.wireOp",EDGE,"E169.MirrorCS"),sQuery(id+"F0.wireOp",EDGE,"E170.MirrorCS"),sQuery(id+"F0.wireOp",EDGE,"E171.MirrorCS"),sQuery(id+"F0.wireOp",EDGE,"E172.MirrorCS"),subQ3,sQuery(id+"F0.wireOp",EDGE,"E174.MirrorCS"),sQuery(id+"F0.wireOp",EDGE,"E175.MirrorCS"),sQuery(id+"F0.wireOp",EDGE,"E176.MirrorCS"),sQuery(id+"F0.wireOp",EDGE,"E177.MirrorCS"),sQuery(id+"F0.wireOp",EDGE,"E178.MirrorCS"),sQuery(id+"F0.wireOp",EDGE,"E179.MirrorCS"),sQuery(id+"F0.wireOp",EDGE,"E180.MirrorCS"),sQuery(id+"F0.wireOp",EDGE,"E181.MirrorCS"),sQuery(id+"F0.wireOp",EDGE,"E182.MirrorCS"),sQuery(id+"F0.wireOp",EDGE,"E183.MirrorCS"),sQuery(id+"F0.wireOp",EDGE,"E184.MirrorCS"),sQuery(id+"F0.wireOp",EDGE,"E185.MirrorCS"),sQuery(id+"F0.wireOp",EDGE,"E186.MirrorCS"),sQuery(id+"F0.wireOp",EDGE,"E187.MirrorCS"),sQuery(id+"F0.wireOp",EDGE,"E188.MirrorCS"),sQuery(id+"F0.wireOp",EDGE,"E189.MirrorCS"),sQuery(id+"F0.wireOp",EDGE,"E190.MirrorCS"),sQuery(id+"F0.wireOp",EDGE,"E191.MirrorCS"),sQuery(id+"F0.wireOp",EDGE,"E192.MirrorCS"),sQuery(id+"F0.wireOp",EDGE,"E193.MirrorCS"),sQuery(id+"F0.wireOp",EDGE,"E194.MirrorCS"),sQuery(id+"F0.wireOp",EDGE,"E195.MirrorCS"),sQuery(id+"F0.wireOp",EDGE,"E196.MirrorCS"),sQuery(id+"F0.wireOp",EDGE,"E197.MirrorCS"),sQuery(id+"F0.wireOp",EDGE,"E198.MirrorCS"),sQuery(id+"F0.wireOp",EDGE,"E199.MirrorCS"),sQuery(id+"F0.wireOp",EDGE,"E200.MirrorCS"),sQuery(id+"F0.wireOp",EDGE,"E201.MirrorCS"),subQ2,sQuery(id+"F0.wireOp",EDGE,"E203.MirrorCS"),sQuery(id+"F0.wireOp",EDGE,"E204.MirrorCS"),sQuery(id+"F0.wireOp",EDGE,"E205.MirrorCS"),sQuery(id+"F0.wireOp",EDGE,"E206.MirrorCS"),sQuery(id+"F0.wireOp",EDGE,"E207.MirrorCS"),sQuery(id+"F0.wireOp",EDGE,"E208.MirrorCS"),sQuery(id+"F0.wireOp",EDGE,"E209.MirrorCS"),sQuery(id+"F0.wireOp",EDGE,"E210.MirrorCS"),subQ1,sQuery(id+"F0.wireOp",EDGE,"E212.MirrorCS"),sQuery(id+"F0.wireOp",EDGE,"E213.MirrorCS"),sQuery(id+"F0.wireOp",EDGE,"E214.MirrorCS"),sQuery(id+"F0.wireOp",EDGE,"E215.MirrorCS"),sQuery(id+"F0.wireOp",EDGE,"E216.MirrorCS"),sQuery(id+"F0.wireOp",EDGE,"E217.MirrorCS"),sQuery(id+"F0.wireOp",EDGE,"E218.MirrorCS"),sQuery(id+"F0.wireOp",EDGE,"E219.MirrorCS"),sQuery(id+"F0.wireOp",EDGE,"E220.MirrorCS"),subQ0,sQuery(id+"F0.wireOp",EDGE,"E222.MirrorCS"),sQuery(id+"F0.wireOp",EDGE,"E223.MirrorCS"),sQuery(id+"F0.wireOp",EDGE,"E224.MirrorCS"),sQuery(id+"F0.wireOp",EDGE,"E225.MirrorCS"),sQuery(id+"F0.wireOp",EDGE,"E226.MirrorCS"),sQuery(id+"F0.wireOp",EDGE,"E227.MirrorCS"),sQuery(id+"F0.wireOp",EDGE,"E228.MirrorCS")])],"isStart":false}),makeQuery(id+"F4.opExtrude","CAP_FACE",FACE,{"disambiguationData":[OSD([subQ3,subQ2,subQ1,subQ0,sQuery(id+"F3.wireOp",EDGE,"E229.bottom"),sQuery(id+"F3.wireOp",EDGE,"E229.left"),sQuery(id+"F3.wireOp",EDGE,"E229.right"),sQuery(id+"F3.wireOp",EDGE,"E230"),sQuery(id+"F3.wireOp",EDGE,"E231"),sQuery(id+"F3.wireOp",EDGE,"E232"),sQuery(id+"F3.wireOp",EDGE,"E233"),sQuery(id+"F3.wireOp",EDGE,"E234"),sQuery(id+"F3.wireOp",EDGE,"E235"),sQuery(id+"F3.wireOp",EDGE,"E236"),sQuery(id+"F3.wireOp",EDGE,"E239.sketch_text.stroke-0"),sQuery(id+"F3.wireOp",EDGE,"E239.sketch_text.stroke-1"),sQuery(id+"F3.wireOp",EDGE,"E239.sketch_text.stroke-2"),sQuery(id+"F3.wireOp",EDGE,"E239.sketch_text.stroke-3"),sQuery(id+"F3.wireOp",EDGE,"E239.sketch_text.stroke-4"),sQuery(id+"F3.wireOp",EDGE,"E239.sketch_text.stroke-5"),sQuery(id+"F3.wireOp",EDGE,"E239.sketch_text.stroke-6"),sQuery(id+"F3.wireOp",EDGE,"E239.sketch_text.stroke-7"),sQuery(id+"F3.wireOp",EDGE,"E239.sketch_text.stroke-8"),sQuery(id+"F3.wireOp",EDGE,"E239.sketch_text.stroke-9"),sQuery(id+"F3.wireOp",EDGE,"E239.sketch_text.stroke-10"),sQuery(id+"F3.wireOp",EDGE,"E239.sketch_text.stroke-11"),sQuery(id+"F3.wireOp",EDGE,"E239.sketch_text.stroke-12"),sQuery(id+"F3.wireOp",EDGE,"E239.sketch_text.stroke-13"),sQuery(id+"F3.wireOp",EDGE,"E239.sketch_text.stroke-14"),sQuery(id+"F3.wireOp",EDGE,"E239.sketch_text.stroke-15"),sQuery(id+"F3.wireOp",EDGE,"E239.sketch_text.stroke-16"),sQuery(id+"F3.wireOp",EDGE,"E239.sketch_text.stroke-17"),sQuery(id+"F3.wireOp",EDGE,"E239.sketch_text.stroke-18"),sQuery(id+"F3.wireOp",EDGE,"E239.sketch_text.stroke-19"),sQuery(id+"F3.wireOp",EDGE,"E239.sketch_text.stroke-20"),sQuery(id+"F3.wireOp",EDGE,"E239.sketch_text.stroke-21"),sQuery(id+"F3.wireOp",EDGE,"E239.sketch_text.stroke-22"),sQuery(id+"F3.wireOp",EDGE,"E239.sketch_text.stroke-23"),sQuery(id+"F3.wireOp",EDGE,"E239.sketch_text.stroke-24"),sQuery(id+"F3.wireOp",EDGE,"E239.sketch_text.stroke-25"),sQuery(id+"F3.wireOp",EDGE,"E239.sketch_text.stroke-26"),sQuery(id+"F3.wireOp",EDGE,"E239.sketch_text.stroke-27"),sQuery(id+"F3.wireOp",EDGE,"E239.sketch_text.stroke-28"),sQuery(id+"F3.wireOp",EDGE,"E239.sketch_text.stroke-29"),sQuery(id+"F3.wireOp",EDGE,"E239.sketch_text.stroke-30"),sQuery(id+"F3.wireOp",EDGE,"E239.sketch_text.stroke-31"),sQuery(id+"F3.wireOp",EDGE,"E239.sketch_text.stroke-32"),sQuery(id+"F3.wireOp",EDGE,"E239.sketch_text.stroke-33"),sQuery(id+"F3.wireOp",EDGE,"E239.sketch_text.stroke-34"),sQuery(id+"F3.wireOp",EDGE,"E239.sketch_text.stroke-35"),sQuery(id+"F3.wireOp",EDGE,"E239.sketch_text.stroke-36"),sQuery(id+"F3.wireOp",EDGE,"E239.sketch_text.stroke-37"),sQuery(id+"F3.wireOp",EDGE,"E239.sketch_text.stroke-38"),sQuery(id+"F3.wireOp",EDGE,"E239.sketch_text.stroke-39"),sQuery(id+"F3.wireOp",EDGE,"E239.sketch_text.stroke-40"),sQuery(id+"F3.wireOp",EDGE,"E239.sketch_text.stroke-41"),sQuery(id+"F3.wireOp",EDGE,"E239.sketch_text.stroke-42"),sQuery(id+"F3.wireOp",EDGE,"E239.sketch_text.stroke-43"),sQuery(id+"F3.wireOp",EDGE,"E239.sketch_text.stroke-44"),sQuery(id+"F3.wireOp",EDGE,"E239.sketch_text.stroke-45"),sQuery(id+"F3.wireOp",EDGE,"E239.sketch_text.stroke-46"),sQuery(id+"F3.wireOp",EDGE,"E239.sketch_text.stroke-47"),sQuery(id+"F3.wireOp",EDGE,"E239.sketch_text.stroke-48"),sQuery(id+"F3.wireOp",EDGE,"E239.sketch_text.stroke-49"),sQuery(id+"F3.wireOp",EDGE,"E239.sketch_text.stroke-50"),sQuery(id+"F3.wireOp",EDGE,"E239.sketch_text.stroke-51"),sQuery(id+"F3.wireOp",EDGE,"E239.sketch_text.stroke-52"),sQuery(id+"F3.wireOp",EDGE,"E239.sketch_text.stroke-53"),sQuery(id+"F3.wireOp",EDGE,"E239.sketch_text.stroke-54"),sQuery(id+"F3.wireOp",EDGE,"E239.sketch_text.stroke-55"),sQuery(id+"F3.wireOp",EDGE,"E239.sketch_text.stroke-56"),sQuery(id+"F3.wireOp",EDGE,"E239.sketch_text.stroke-57"),sQuery(id+"F3.wireOp",EDGE,"E239.sketch_text.stroke-58"),sQuery(id+"F3.wireOp",EDGE,"E239.sketch_text.stroke-59"),sQuery(id+"F3.wireOp",EDGE,"E239.sketch_text.stroke-60"),sQuery(id+"F3.wireOp",EDGE,"E239.sketch_text.stroke-61"),sQuery(id+"F3.wireOp",EDGE,"E239.sketch_text.stroke-62"),sQuery(id+"F3.wireOp",EDGE,"E239.sketch_text.stroke-63"),sQuery(id+"F3.wireOp",EDGE,"E239.sketch_text.stroke-64"),sQuery(id+"F3.wireOp",EDGE,"E239.sketch_text.stroke-65"),sQuery(id+"F3.wireOp",EDGE,"E239.sketch_text.stroke-66"),sQuery(id+"F3.wireOp",EDGE,"E239.sketch_text.stroke-67"),sQuery(id+"F3.wireOp",EDGE,"E239.sketch_text.stroke-68"),sQuery(id+"F3.wireOp",EDGE,"E239.sketch_text.stroke-69"),sQuery(id+"F3.wireOp",EDGE,"E239.sketch_text.stroke-70"),sQuery(id+"F3.wireOp",EDGE,"E239.sketch_text.stroke-71"),sQuery(id+"F3.wireOp",EDGE,"E239.sketch_text.stroke-72"),sQuery(id+"F3.wireOp",EDGE,"E239.sketch_text.stroke-73"),sQuery(id+"F3.wireOp",EDGE,"E239.sketch_text.stroke-74"),sQuery(id+"F3.wireOp",EDGE,"E239.sketch_text.stroke-75"),sQuery(id+"F3.wireOp",EDGE,"E239.sketch_text.stroke-76"),sQuery(id+"F3.wireOp",EDGE,"E239.sketch_text.stroke-77"),sQuery(id+"F3.wireOp",EDGE,"E239.sketch_text.stroke-78"),sQuery(id+"F3.wireOp",EDGE,"E239.sketch_text.stroke-79"),sQuery(id+"F3.wireOp",EDGE,"E239.sketch_text.stroke-80"),sQuery(id+"F3.wireOp",EDGE,"E239.sketch_text.stroke-81"),sQuery(id+"F3.wireOp",EDGE,"E239.sketch_text.stroke-82"),sQuery(id+"F3.wireOp",EDGE,"E239.sketch_text.stroke-83"),sQuery(id+"F3.wireOp",EDGE,"E239.sketch_text.stroke-84"),sQuery(id+"F3.wireOp",EDGE,"E239.sketch_text.stroke-85"),sQuery(id+"F3.wireOp",EDGE,"E239.sketch_text.stroke-86"),sQuery(id+"F3.wireOp",EDGE,"E239.sketch_text.stroke-87"),sQuery(id+"F3.wireOp",EDGE,"E239.sketch_text.stroke-101"),sQuery(id+"F3.wireOp",EDGE,"E239.sketch_text.stroke-102"),sQuery(id+"F3.wireOp",EDGE,"E239.sketch_text.stroke-103"),sQuery(id+"F3.wireOp",EDGE,"E239.sketch_text.stroke-104"),sQuery(id+"F3.wireOp",EDGE,"E239.sketch_text.stroke-105"),sQuery(id+"F3.wireOp",EDGE,"E239.sketch_text.stroke-106"),sQuery(id+"F3.wireOp",EDGE,"E239.sketch_text.stroke-107"),sQuery(id+"F3.wireOp",EDGE,"E239.sketch_text.stroke-108"),sQuery(id+"F3.wireOp",EDGE,"E239.sketch_text.stroke-109"),sQuery(id+"F3.wireOp",EDGE,"E239.sketch_text.stroke-110"),sQuery(id+"F3.wireOp",EDGE,"E239.sketch_text.stroke-111"),sQuery(id+"F3.wireOp",EDGE,"E239.sketch_text.stroke-112"),sQuery(id+"F3.wireOp",EDGE,"E239.sketch_text.stroke-113"),sQuery(id+"F3.wireOp",EDGE,"E239.sketch_text.stroke-114"),sQuery(id+"F3.wireOp",EDGE,"E239.sketch_text.stroke-115"),sQuery(id+"F3.wireOp",EDGE,"E239.sketch_text.stroke-116"),sQuery(id+"F3.wireOp",EDGE,"E239.sketch_text.stroke-117"),sQuery(id+"F3.wireOp",EDGE,"E239.sketch_text.stroke-118"),sQuery(id+"F3.wireOp",EDGE,"E239.sketch_text.stroke-119"),sQuery(id+"F3.wireOp",EDGE,"E239.sketch_text.stroke-120"),sQuery(id+"F3.wireOp",EDGE,"E239.sketch_text.stroke-121"),sQuery(id+"F3.wireOp",EDGE,"E239.sketch_text.stroke-122"),sQuery(id+"F3.wireOp",EDGE,"E239.sketch_text.stroke-123"),sQuery(id+"F3.wireOp",EDGE,"E239.sketch_text.stroke-124"),sQuery(id+"F3.wireOp",EDGE,"E239.sketch_text.stroke-125"),sQuery(id+"F3.wireOp",EDGE,"E239.sketch_text.stroke-126"),sQuery(id+"F3.wireOp",EDGE,"E239.sketch_text.stroke-127"),sQuery(id+"F3.wireOp",EDGE,"E239.sketch_text.stroke-128"),sQuery(id+"F3.wireOp",EDGE,"E239.sketch_text.stroke-129"),sQuery(id+"F3.wireOp",EDGE,"E239.sketch_text.stroke-130"),sQuery(id+"F3.wireOp",EDGE,"E239.sketch_text.stroke-131"),sQuery(id+"F3.wireOp",EDGE,"E239.sketch_text.stroke-132"),sQuery(id+"F3.wireOp",EDGE,"E239.sketch_text.stroke-133"),sQuery(id+"F3.wireOp",EDGE,"E239.sketch_text.stroke-134"),sQuery(id+"F3.wireOp",EDGE,"E239.sketch_text.stroke-135"),sQuery(id+"F3.wireOp",EDGE,"E239.sketch_text.stroke-136"),sQuery(id+"F3.wireOp",EDGE,"E239.sketch_text.stroke-137"),sQuery(id+"F3.wireOp",EDGE,"E239.sketch_text.stroke-138"),sQuery(id+"F3.wireOp",EDGE,"E239.sketch_text.stroke-139"),sQuery(id+"F3.wireOp",EDGE,"E239.sketch_text.stroke-144"),sQuery(id+"F3.wireOp",EDGE,"E239.sketch_text.stroke-145"),sQuery(id+"F3.wireOp",EDGE,"E239.sketch_text.stroke-146"),sQuery(id+"F3.wireOp",EDGE,"E239.sketch_text.stroke-147"),sQuery(id+"F3.wireOp",EDGE,"E239.sketch_text.stroke-148"),sQuery(id+"F3.wireOp",EDGE,"E239.sketch_text.stroke-149"),sQuery(id+"F3.wireOp",EDGE,"E239.sketch_text.stroke-150"),sQuery(id+"F3.wireOp",EDGE,"E239.sketch_text.stroke-151"),sQuery(id+"F3.wireOp",EDGE,"E239.sketch_text.stroke-152"),sQuery(id+"F3.wireOp",EDGE,"E239.sketch_text.stroke-153"),sQuery(id+"F3.wireOp",EDGE,"E239.sketch_text.stroke-154"),sQuery(id+"F3.wireOp",EDGE,"E239.sketch_text.stroke-155"),sQuery(id+"F3.wireOp",EDGE,"E239.sketch_text.stroke-156"),sQuery(id+"F3.wireOp",EDGE,"E239.sketch_text.stroke-157"),sQuery(id+"F3.wireOp",EDGE,"E239.sketch_text.stroke-158"),sQuery(id+"F3.wireOp",EDGE,"E239.sketch_text.stroke-159"),sQuery(id+"F3.wireOp",EDGE,"E239.sketch_text.stroke-160"),sQuery(id+"F3.wireOp",EDGE,"E239.sketch_text.stroke-161"),sQuery(id+"F3.wireOp",EDGE,"E239.sketch_text.stroke-162"),sQuery(id+"F3.wireOp",EDGE,"E239.sketch_text.stroke-163"),sQuery(id+"F3.wireOp",EDGE,"E239.sketch_text.stroke-164"),sQuery(id+"F3.wireOp",EDGE,"E239.sketch_text.stroke-170"),sQuery(id+"F3.wireOp",EDGE,"E239.sketch_text.stroke-171"),sQuery(id+"F3.wireOp",EDGE,"E239.sketch_text.stroke-172"),sQuery(id+"F3.wireOp",EDGE,"E239.sketch_text.stroke-173"),sQuery(id+"F3.wireOp",EDGE,"E239.sketch_text.stroke-174"),sQuery(id+"F3.wireOp",EDGE,"E239.sketch_text.stroke-175"),sQuery(id+"F3.wireOp",EDGE,"E239.sketch_text.stroke-176"),sQuery(id+"F3.wireOp",EDGE,"E239.sketch_text.stroke-177"),sQuery(id+"F3.wireOp",EDGE,"E239.sketch_text.stroke-178"),sQuery(id+"F3.wireOp",EDGE,"E240"),sQuery(id+"F3.wireOp",EDGE,"E241"),sQuery(id+"F3.wireOp",EDGE,"E242"),sQuery(id+"F3.wireOp",EDGE,"E243.0"),sQuery(id+"F3.wireOp",EDGE,"E243.1"),sQuery(id+"F3.wireOp",EDGE,"E243.2")])],"isStart":true})]});}
            var sketch = newSketch(context, id + "F7", { "sketchPlane" : qUnion([Q0])});
            skLineSegment(sketch, "E244.bottom", {"start": v(0.86, -44.1) * mm, "end": v(2.06, -44.1) * mm});
            skLineSegment(sketch, "E244.top", {"start": v(0.86, -54.31) * mm, "end": v(2.06, -54.31) * mm});
            skLineSegment(sketch, "E244.left", {"start": v(0.86, -44.1) * mm, "end": v(0.86, -54.31) * mm});
            skLineSegment(sketch, "E244.right", {"start": v(2.06, -44.1) * mm, "end": v(2.06, -54.31) * mm});
            skLineSegment(sketch, "E245.bottom", {"start": v(10.33, -44.1) * mm, "end": v(11.44, -44.1) * mm});
            skLineSegment(sketch, "E245.top", {"start": v(10.33, -50.37) * mm, "end": v(11.44, -50.37) * mm});
            skLineSegment(sketch, "E245.left", {"start": v(10.33, -44.1) * mm, "end": v(10.33, -50.37) * mm});
            skLineSegment(sketch, "E245.right", {"start": v(11.44, -44.1) * mm, "end": v(11.44, -50.37) * mm});
            skLineSegment(sketch, "E246.bottom", {"start": v(33.43, -44.22) * mm, "end": v(34.63, -44.22) * mm});
            skLineSegment(sketch, "E246.top", {"start": v(33.43, -51.81) * mm, "end": v(34.63, -51.81) * mm});
            skLineSegment(sketch, "E246.left", {"start": v(33.43, -44.22) * mm, "end": v(33.43, -51.81) * mm});
            skLineSegment(sketch, "E246.right", {"start": v(34.63, -44.22) * mm, "end": v(34.63, -51.81) * mm});
            skLineSegment(sketch, "E247.bottom", {"start": v(53.46, -44.26) * mm, "end": v(54.66, -44.26) * mm});
            skLineSegment(sketch, "E247.top", {"start": v(53.46, -54.17) * mm, "end": v(54.66, -54.17) * mm});
            skLineSegment(sketch, "E247.left", {"start": v(53.46, -44.26) * mm, "end": v(53.46, -54.17) * mm});
            skLineSegment(sketch, "E247.right", {"start": v(54.66, -44.26) * mm, "end": v(54.66, -54.17) * mm});
            skSolve(sketch);
        }
        {
            var Q0;
            {var subQ5=sQuery(id+"F7.wireOp",EDGE,"E244.left");var subQ9=makeQuery(id+"F4.opExtrude","CAP_EDGE",EDGE,{"disambiguationData":[OSD([sQuery(id+"F3.wireOp",EDGE,"E239.sketch_text.stroke-85")])],"isStart":true});var subQ10=makeQuery(id+"F7.imprint","INTERSECT",VERTEX,{"derivedFrom":[subQ9,subQ5]});Q0=makeQuery(id+"F7.imprint","IMPRINT",FACE,{"disambiguationData":[TD([[makeQuery(id+"F7.imprint","IMPRINT",EDGE,{"disambiguationData":[TD([[subQ10,-1.0]])],"derivedFrom":subQ5}),1.0]])]});}
            var Q1;
            {var subQ6=sQuery(id+"F7.wireOp",EDGE,"E245.top");Q1=makeQuery(id+"F7.imprint","IMPRINT",FACE,{"disambiguationData":[TD([[makeQuery(id+"F7.imprint","IMPRINT",EDGE,{"derivedFrom":subQ6}),-1.0]])]});}
            var Q2;
            Q2=makeQuery(id+"F7.imprint","IMPRINT",FACE,{"disambiguationData":[TD([[makeQuery(id+"F7.imprint","IMPRINT",EDGE,{"derivedFrom":sQuery(id+"F7.wireOp",EDGE,"E246.bottom")}),-1.0]])]});
            var Q3;
            {var subQ0=sQuery(id+"F7.wireOp",EDGE,"E247.left");Q3=makeQuery(id+"F7.imprint","IMPRINT",FACE,{"disambiguationData":[TD([[makeQuery(id+"F7.imprint","IMPRINT",EDGE,{"derivedFrom":subQ0}),1.0]])]});}
            var Q4;
            {var subQ0=sQuery(id+"F0.wireOp",EDGE,"E228.MirrorCS");var subQ1=sQuery(id+"F0.wireOp",EDGE,"E227.MirrorCS");var subQ2=sQuery(id+"F0.wireOp",EDGE,"E226.MirrorCS");var subQ3=sQuery(id+"F0.wireOp",EDGE,"E225.MirrorCS");var subQ4=sQuery(id+"F0.wireOp",EDGE,"E224.MirrorCS");var subQ5=sQuery(id+"F0.wireOp",EDGE,"E223.MirrorCS");var subQ6=sQuery(id+"F0.wireOp",EDGE,"E222.MirrorCS");var subQ7=sQuery(id+"F0.wireOp",EDGE,"E221.MirrorCS");var subQ8=sQuery(id+"F0.wireOp",EDGE,"E220.MirrorCS");var subQ9=sQuery(id+"F0.wireOp",EDGE,"E219.MirrorCS");var subQ10=sQuery(id+"F0.wireOp",EDGE,"E218.MirrorCS");var subQ11=sQuery(id+"F0.wireOp",EDGE,"E217.MirrorCS");var subQ12=sQuery(id+"F0.wireOp",EDGE,"E216.MirrorCS");var subQ13=sQuery(id+"F0.wireOp",EDGE,"E215.MirrorCS");var subQ14=sQuery(id+"F0.wireOp",EDGE,"E214.MirrorCS");var subQ15=sQuery(id+"F0.wireOp",EDGE,"E213.MirrorCS");var subQ16=sQuery(id+"F0.wireOp",EDGE,"E212.MirrorCS");var subQ17=sQuery(id+"F0.wireOp",EDGE,"E211.MirrorCS");var subQ18=sQuery(id+"F0.wireOp",EDGE,"E210.MirrorCS");var subQ19=sQuery(id+"F0.wireOp",EDGE,"E209.MirrorCS");var subQ20=sQuery(id+"F0.wireOp",EDGE,"E208.MirrorCS");var subQ21=sQuery(id+"F0.wireOp",EDGE,"E207.MirrorCS");var subQ22=sQuery(id+"F0.wireOp",EDGE,"E206.MirrorCS");var subQ23=sQuery(id+"F0.wireOp",EDGE,"E205.MirrorCS");var subQ24=sQuery(id+"F0.wireOp",EDGE,"E204.MirrorCS");var subQ25=sQuery(id+"F0.wireOp",EDGE,"E203.MirrorCS");var subQ26=sQuery(id+"F0.wireOp",EDGE,"E202.MirrorCS");var subQ27=sQuery(id+"F0.wireOp",EDGE,"E201.MirrorCS");var subQ28=sQuery(id+"F0.wireOp",EDGE,"E200.MirrorCS");var subQ29=sQuery(id+"F0.wireOp",EDGE,"E199.MirrorCS");var subQ30=sQuery(id+"F0.wireOp",EDGE,"E198.MirrorCS");var subQ31=sQuery(id+"F0.wireOp",EDGE,"E197.MirrorCS");var subQ32=sQuery(id+"F0.wireOp",EDGE,"E196.MirrorCS");var subQ33=sQuery(id+"F0.wireOp",EDGE,"E195.MirrorCS");var subQ34=sQuery(id+"F0.wireOp",EDGE,"E194.MirrorCS");var subQ35=sQuery(id+"F0.wireOp",EDGE,"E193.MirrorCS");var subQ36=sQuery(id+"F0.wireOp",EDGE,"E192.MirrorCS");var subQ37=sQuery(id+"F0.wireOp",EDGE,"E191.MirrorCS");var subQ38=sQuery(id+"F0.wireOp",EDGE,"E190.MirrorCS");var subQ39=sQuery(id+"F0.wireOp",EDGE,"E189.MirrorCS");var subQ40=sQuery(id+"F0.wireOp",EDGE,"E188.MirrorCS");var subQ41=sQuery(id+"F0.wireOp",EDGE,"E187.MirrorCS");var subQ42=sQuery(id+"F0.wireOp",EDGE,"E186.MirrorCS");var subQ43=sQuery(id+"F0.wireOp",EDGE,"E185.MirrorCS");var subQ44=sQuery(id+"F0.wireOp",EDGE,"E184.MirrorCS");var subQ45=sQuery(id+"F0.wireOp",EDGE,"E183.MirrorCS");var subQ46=sQuery(id+"F0.wireOp",EDGE,"E182.MirrorCS");var subQ47=sQuery(id+"F0.wireOp",EDGE,"E181.MirrorCS");var subQ48=sQuery(id+"F0.wireOp",EDGE,"E180.MirrorCS");var subQ49=sQuery(id+"F0.wireOp",EDGE,"E179.MirrorCS");var subQ50=sQuery(id+"F0.wireOp",EDGE,"E178.MirrorCS");var subQ51=sQuery(id+"F0.wireOp",EDGE,"E177.MirrorCS");var subQ52=sQuery(id+"F0.wireOp",EDGE,"E176.MirrorCS");var subQ53=sQuery(id+"F0.wireOp",EDGE,"E175.MirrorCS");var subQ54=sQuery(id+"F0.wireOp",EDGE,"E174.MirrorCS");var subQ55=sQuery(id+"F0.wireOp",EDGE,"E173.MirrorCS");var subQ56=sQuery(id+"F0.wireOp",EDGE,"E172.MirrorCS");var subQ57=sQuery(id+"F0.wireOp",EDGE,"E171.MirrorCS");var subQ58=sQuery(id+"F0.wireOp",EDGE,"E170.MirrorCS");var subQ59=sQuery(id+"F0.wireOp",EDGE,"E169.MirrorCS");var subQ60=sQuery(id+"F0.wireOp",EDGE,"E168.MirrorCS");var subQ61=sQuery(id+"F0.wireOp",EDGE,"E167.MirrorCS");var subQ62=sQuery(id+"F0.wireOp",EDGE,"E166.MirrorCS");var subQ63=sQuery(id+"F0.wireOp",EDGE,"E165.MirrorCS");var subQ64=sQuery(id+"F0.wireOp",EDGE,"E164.MirrorCS");var subQ65=sQuery(id+"F0.wireOp",EDGE,"E163.MirrorCS");var subQ66=sQuery(id+"F0.wireOp",EDGE,"E162.MirrorCS");var subQ67=sQuery(id+"F0.wireOp",EDGE,"E161.MirrorCS");var subQ68=sQuery(id+"F0.wireOp",EDGE,"E160.MirrorCS");var subQ69=sQuery(id+"F0.wireOp",EDGE,"E159.MirrorCS");var subQ70=sQuery(id+"F0.wireOp",EDGE,"E158.MirrorCS");var subQ71=sQuery(id+"F0.wireOp",EDGE,"E157.MirrorCS");var subQ72=sQuery(id+"F0.wireOp",EDGE,"E156.MirrorCS");var subQ73=sQuery(id+"F0.wireOp",EDGE,"E155.MirrorCS");var subQ74=sQuery(id+"F0.wireOp",EDGE,"E154.MirrorCS");var subQ75=sQuery(id+"F0.wireOp",EDGE,"E153.MirrorCS");var subQ76=sQuery(id+"F0.wireOp",EDGE,"E152.MirrorCS");var subQ77=sQuery(id+"F0.wireOp",EDGE,"E151.MirrorCS");var subQ78=sQuery(id+"F0.wireOp",EDGE,"E150.MirrorCS");var subQ79=sQuery(id+"F0.wireOp",EDGE,"E149.MirrorCS");var subQ80=sQuery(id+"F0.wireOp",EDGE,"E148.MirrorCS");var subQ81=sQuery(id+"F0.wireOp",EDGE,"E147.MirrorCS");var subQ82=sQuery(id+"F0.wireOp",EDGE,"E146.MirrorCS");var subQ83=sQuery(id+"F0.wireOp",EDGE,"E145.MirrorCS");var subQ84=sQuery(id+"F0.wireOp",EDGE,"E144.MirrorCS");var subQ85=sQuery(id+"F0.wireOp",EDGE,"E143.MirrorCS");var subQ86=sQuery(id+"F0.wireOp",EDGE,"E142.MirrorCS");var subQ87=sQuery(id+"F0.wireOp",EDGE,"E141.MirrorCS");var subQ88=sQuery(id+"F0.wireOp",EDGE,"E140.MirrorCS");var subQ89=sQuery(id+"F0.wireOp",EDGE,"E139.MirrorCS");var subQ90=sQuery(id+"F0.wireOp",EDGE,"E138.MirrorCS");var subQ91=sQuery(id+"F0.wireOp",EDGE,"E137.MirrorCS");var subQ92=sQuery(id+"F0.wireOp",EDGE,"E136.MirrorCS");var subQ93=sQuery(id+"F0.wireOp",EDGE,"E135.MirrorCS");var subQ94=sQuery(id+"F0.wireOp",EDGE,"E134.MirrorCS");var subQ95=sQuery(id+"F0.wireOp",EDGE,"E133.MirrorCS");var subQ96=sQuery(id+"F0.wireOp",EDGE,"E132.MirrorCS");var subQ97=sQuery(id+"F0.wireOp",EDGE,"E131.MirrorCS");var subQ98=sQuery(id+"F0.wireOp",EDGE,"E130.MirrorCS");var subQ99=sQuery(id+"F0.wireOp",EDGE,"E129.MirrorCS");var subQ100=sQuery(id+"F0.wireOp",EDGE,"E128.MirrorCS");var subQ101=sQuery(id+"F0.wireOp",EDGE,"E127.MirrorCS");var subQ102=sQuery(id+"F0.wireOp",EDGE,"E126.MirrorCS");var subQ103=sQuery(id+"F0.wireOp",EDGE,"E125.MirrorCS");var subQ104=sQuery(id+"F0.wireOp",EDGE,"E124.MirrorCS");var subQ105=sQuery(id+"F0.wireOp",EDGE,"E123.MirrorCS");var subQ106=sQuery(id+"F0.wireOp",EDGE,"E122.MirrorCS");var subQ107=sQuery(id+"F0.wireOp",EDGE,"E121.MirrorCS");var subQ108=sQuery(id+"F0.wireOp",EDGE,"E120.MirrorCS");var subQ109=sQuery(id+"F0.wireOp",EDGE,"E119.MirrorCS");var subQ110=sQuery(id+"F0.wireOp",EDGE,"E118.MirrorCS");var subQ111=sQuery(id+"F0.wireOp",EDGE,"E117.MirrorCS");var subQ112=sQuery(id+"F0.wireOp",EDGE,"E116.MirrorCS");var subQ113=sQuery(id+"F0.wireOp",EDGE,"E115.MirrorCS");var subQ114=sQuery(id+"F0.wireOp",EDGE,"E114");var subQ115=sQuery(id+"F0.wireOp",EDGE,"E113");var subQ116=sQuery(id+"F0.wireOp",EDGE,"E112");var subQ117=sQuery(id+"F0.wireOp",EDGE,"E111");var subQ118=sQuery(id+"F0.wireOp",EDGE,"E110");var subQ119=sQuery(id+"F0.wireOp",EDGE,"E109");var subQ120=sQuery(id+"F0.wireOp",EDGE,"E108");var subQ121=sQuery(id+"F0.wireOp",EDGE,"E107");var subQ122=sQuery(id+"F0.wireOp",EDGE,"E106");var subQ123=sQuery(id+"F0.wireOp",EDGE,"E105");var subQ124=sQuery(id+"F0.wireOp",EDGE,"E104");var subQ125=sQuery(id+"F0.wireOp",EDGE,"E103");var subQ126=sQuery(id+"F0.wireOp",EDGE,"E102");var subQ127=sQuery(id+"F0.wireOp",EDGE,"E101");var subQ128=sQuery(id+"F0.wireOp",EDGE,"E100");var subQ129=sQuery(id+"F0.wireOp",EDGE,"E99");var subQ130=sQuery(id+"F0.wireOp",EDGE,"E98");var subQ131=sQuery(id+"F0.wireOp",EDGE,"E97");var subQ132=sQuery(id+"F0.wireOp",EDGE,"E96");var subQ133=sQuery(id+"F0.wireOp",EDGE,"E95");var subQ134=sQuery(id+"F0.wireOp",EDGE,"E94");var subQ135=sQuery(id+"F0.wireOp",EDGE,"E93");var subQ136=sQuery(id+"F0.wireOp",EDGE,"E92");var subQ137=sQuery(id+"F0.wireOp",EDGE,"E91");var subQ138=sQuery(id+"F0.wireOp",EDGE,"E90");var subQ139=sQuery(id+"F0.wireOp",EDGE,"E89");var subQ140=sQuery(id+"F0.wireOp",EDGE,"E88");var subQ141=sQuery(id+"F0.wireOp",EDGE,"E87");var subQ142=sQuery(id+"F0.wireOp",EDGE,"E86");var subQ143=sQuery(id+"F0.wireOp",EDGE,"E85");var subQ144=sQuery(id+"F0.wireOp",EDGE,"E84");var subQ145=sQuery(id+"F0.wireOp",EDGE,"E83");var subQ146=sQuery(id+"F0.wireOp",EDGE,"E82");var subQ147=sQuery(id+"F0.wireOp",EDGE,"E81");var subQ148=sQuery(id+"F0.wireOp",EDGE,"E80");var subQ149=sQuery(id+"F0.wireOp",EDGE,"E79");var subQ150=sQuery(id+"F0.wireOp",EDGE,"E78");var subQ151=sQuery(id+"F0.wireOp",EDGE,"E77");var subQ152=sQuery(id+"F0.wireOp",EDGE,"E76");var subQ153=sQuery(id+"F0.wireOp",EDGE,"E75");var subQ154=sQuery(id+"F0.wireOp",EDGE,"E74");var subQ155=sQuery(id+"F0.wireOp",EDGE,"E73");var subQ156=sQuery(id+"F0.wireOp",EDGE,"E72");var subQ157=sQuery(id+"F0.wireOp",EDGE,"E71");var subQ158=sQuery(id+"F0.wireOp",EDGE,"E70");var subQ159=sQuery(id+"F0.wireOp",EDGE,"E69");var subQ160=sQuery(id+"F0.wireOp",EDGE,"E68");var subQ161=sQuery(id+"F0.wireOp",EDGE,"E67");var subQ162=sQuery(id+"F0.wireOp",EDGE,"E66");var subQ163=sQuery(id+"F0.wireOp",EDGE,"E65");var subQ164=sQuery(id+"F0.wireOp",EDGE,"E64");var subQ165=sQuery(id+"F0.wireOp",EDGE,"E63");var subQ166=sQuery(id+"F0.wireOp",EDGE,"E62");var subQ167=sQuery(id+"F0.wireOp",EDGE,"E61");var subQ168=sQuery(id+"F0.wireOp",EDGE,"E60");var subQ169=sQuery(id+"F0.wireOp",EDGE,"E59");var subQ170=sQuery(id+"F0.wireOp",EDGE,"E58");var subQ171=sQuery(id+"F0.wireOp",EDGE,"E57");var subQ172=sQuery(id+"F0.wireOp",EDGE,"E56");var subQ173=sQuery(id+"F0.wireOp",EDGE,"E55");var subQ174=sQuery(id+"F0.wireOp",EDGE,"E54");var subQ175=sQuery(id+"F0.wireOp",EDGE,"E53");var subQ176=sQuery(id+"F0.wireOp",EDGE,"E52");var subQ177=sQuery(id+"F0.wireOp",EDGE,"E51");var subQ178=sQuery(id+"F0.wireOp",EDGE,"E50");var subQ179=sQuery(id+"F0.wireOp",EDGE,"E49");var subQ180=sQuery(id+"F0.wireOp",EDGE,"E48");var subQ181=sQuery(id+"F0.wireOp",EDGE,"E47");var subQ182=sQuery(id+"F0.wireOp",EDGE,"E46");var subQ183=sQuery(id+"F0.wireOp",EDGE,"E45");var subQ184=sQuery(id+"F0.wireOp",EDGE,"E44");var subQ185=sQuery(id+"F0.wireOp",EDGE,"E43");var subQ186=sQuery(id+"F0.wireOp",EDGE,"E42");var subQ187=sQuery(id+"F0.wireOp",EDGE,"E41");var subQ188=sQuery(id+"F0.wireOp",EDGE,"E40");var subQ189=sQuery(id+"F0.wireOp",EDGE,"E39");var subQ190=sQuery(id+"F0.wireOp",EDGE,"E38");var subQ191=sQuery(id+"F0.wireOp",EDGE,"E37");var subQ192=sQuery(id+"F0.wireOp",EDGE,"E36");var subQ193=sQuery(id+"F0.wireOp",EDGE,"E35");var subQ194=sQuery(id+"F0.wireOp",EDGE,"E34");var subQ195=sQuery(id+"F0.wireOp",EDGE,"E33");var subQ196=sQuery(id+"F0.wireOp",EDGE,"E32");var subQ197=sQuery(id+"F0.wireOp",EDGE,"E31");var subQ198=sQuery(id+"F0.wireOp",EDGE,"E30");var subQ199=sQuery(id+"F0.wireOp",EDGE,"E29");var subQ200=sQuery(id+"F0.wireOp",EDGE,"E28");var subQ201=sQuery(id+"F0.wireOp",EDGE,"E27");var subQ202=sQuery(id+"F0.wireOp",EDGE,"E26");var subQ203=sQuery(id+"F0.wireOp",EDGE,"E25");var subQ204=sQuery(id+"F0.wireOp",EDGE,"E24");var subQ205=sQuery(id+"F0.wireOp",EDGE,"E23");var subQ206=sQuery(id+"F0.wireOp",EDGE,"E22");var subQ207=sQuery(id+"F0.wireOp",EDGE,"E21");var subQ208=sQuery(id+"F0.wireOp",EDGE,"E20");var subQ209=sQuery(id+"F0.wireOp",EDGE,"E19");var subQ210=sQuery(id+"F0.wireOp",EDGE,"E18");var subQ211=sQuery(id+"F0.wireOp",EDGE,"E17");var subQ212=sQuery(id+"F0.wireOp",EDGE,"E16");var subQ213=sQuery(id+"F0.wireOp",EDGE,"E15");var subQ214=sQuery(id+"F0.wireOp",EDGE,"E14");var subQ215=sQuery(id+"F0.wireOp",EDGE,"E13");var subQ216=sQuery(id+"F0.wireOp",EDGE,"E12");var subQ217=sQuery(id+"F0.wireOp",EDGE,"E11");var subQ218=sQuery(id+"F0.wireOp",EDGE,"E10");var subQ219=sQuery(id+"F0.wireOp",EDGE,"E9");var subQ220=sQuery(id+"F0.wireOp",EDGE,"E8");var subQ221=sQuery(id+"F0.wireOp",EDGE,"E7");var subQ222=sQuery(id+"F0.wireOp",EDGE,"E6");var subQ223=sQuery(id+"F0.wireOp",EDGE,"E5");var subQ224=sQuery(id+"F0.wireOp",EDGE,"E4");var subQ225=sQuery(id+"F0.wireOp",EDGE,"E3");var subQ226=sQuery(id+"F0.wireOp",EDGE,"E2");var subQ227=sQuery(id+"F0.wireOp",EDGE,"E1");Q4=makeQuery(id+"F4.boolean.opBoolean","MERGE",FACE,{"derivedFrom":[makeQuery(id+"F1.opExtrude","CAP_FACE",FACE,{"disambiguationData":[OSD([subQ227,subQ226,subQ225,subQ224,subQ223,subQ222,subQ221,subQ220,subQ219,subQ218,subQ217,subQ216,subQ215,subQ214,subQ213,subQ212,subQ211,subQ210,subQ209,subQ208,subQ207,subQ206,subQ205,subQ204,subQ203,subQ202,subQ201,subQ200,subQ199,subQ198,subQ197,subQ196,subQ195,subQ194,subQ193,subQ192,subQ191,subQ190,subQ189,subQ188,subQ187,subQ186,subQ185,subQ184,subQ183,subQ182,subQ181,subQ180,subQ179,subQ178,subQ177,subQ176,subQ175,subQ174,subQ173,subQ172,subQ171,subQ170,subQ169,subQ168,subQ167,subQ166,subQ165,subQ164,subQ163,subQ162,subQ161,subQ160,subQ159,subQ158,subQ157,subQ156,subQ155,subQ154,subQ153,subQ152,subQ151,subQ150,subQ149,subQ148,subQ147,subQ146,subQ145,subQ144,subQ143,subQ142,subQ141,subQ140,subQ139,subQ138,subQ137,subQ136,subQ135,subQ134,subQ133,subQ132,subQ131,subQ130,subQ129,subQ128,subQ127,subQ126,subQ125,subQ124,subQ123,subQ122,subQ121,subQ120,subQ119,subQ118,subQ117,subQ116,subQ115,subQ114,subQ113,subQ112,subQ111,subQ110,subQ109,subQ108,subQ107,subQ106,subQ105,subQ104,subQ103,subQ102,subQ101,subQ100,subQ99,subQ98,subQ97,subQ96,subQ95,subQ94,subQ93,subQ92,subQ91,subQ90,subQ89,subQ88,subQ87,subQ86,subQ85,subQ84,subQ83,subQ82,subQ81,subQ80,subQ79,subQ78,subQ77,subQ76,subQ75,subQ74,subQ73,subQ72,subQ71,subQ70,subQ69,subQ68,subQ67,subQ66,subQ65,subQ64,subQ63,subQ62,subQ61,subQ60,subQ59,subQ58,subQ57,subQ56,subQ55,subQ54,subQ53,subQ52,subQ51,subQ50,subQ49,subQ48,subQ47,subQ46,subQ45,subQ44,subQ43,subQ42,subQ41,subQ40,subQ39,subQ38,subQ37,subQ36,subQ35,subQ34,subQ33,subQ32,subQ31,subQ30,subQ29,subQ28,subQ27,subQ26,subQ25,subQ24,subQ23,subQ22,subQ21,subQ20,subQ19,subQ18,subQ17,subQ16,subQ15,subQ14,subQ13,subQ12,subQ11,subQ10,subQ9,subQ8,subQ7,subQ6,subQ5,subQ4,subQ3,subQ2,subQ1,subQ0])],"isStart":true}),makeQuery(id+"F4.opExtrude","CAP_FACE",FACE,{"disambiguationData":[OSD([subQ227,subQ226,subQ225,subQ224,subQ223,subQ222,subQ221,subQ220,subQ219,subQ218,subQ217,subQ216,subQ215,subQ214,subQ213,subQ212,subQ211,subQ210,subQ209,subQ208,subQ207,subQ206,subQ205,subQ204,subQ203,subQ202,subQ201,subQ200,subQ199,subQ198,subQ197,subQ196,subQ195,subQ194,subQ193,subQ192,subQ191,subQ190,subQ189,subQ188,subQ187,subQ186,subQ185,subQ184,subQ183,subQ182,subQ181,subQ180,subQ179,subQ178,subQ177,subQ176,subQ175,subQ174,subQ173,subQ172,subQ171,subQ170,subQ169,subQ168,subQ167,subQ166,subQ165,subQ164,subQ163,subQ162,subQ161,subQ160,subQ159,subQ158,subQ157,subQ156,subQ155,subQ154,subQ153,subQ152,subQ151,subQ150,subQ149,subQ148,subQ147,subQ146,subQ145,subQ144,subQ143,subQ142,subQ141,subQ140,subQ139,subQ138,subQ137,subQ136,subQ135,subQ134,subQ133,subQ132,subQ131,subQ130,subQ129,subQ128,subQ127,subQ126,subQ125,subQ124,subQ123,subQ122,subQ121,subQ120,subQ119,subQ118,subQ117,subQ116,subQ115,subQ114,subQ113,subQ112,subQ111,subQ110,subQ109,subQ108,subQ107,subQ106,subQ105,subQ104,subQ103,subQ102,subQ101,subQ100,subQ99,subQ98,subQ97,subQ96,subQ95,subQ94,subQ93,subQ92,subQ91,subQ90,subQ89,subQ88,subQ87,subQ86,subQ85,subQ84,subQ83,subQ82,subQ81,subQ80,subQ79,subQ78,subQ77,subQ76,subQ75,subQ74,subQ73,subQ72,subQ71,subQ70,subQ69,subQ68,subQ67,subQ66,subQ65,subQ64,subQ63,subQ62,subQ61,subQ60,subQ59,subQ58,subQ57,subQ56,subQ55,subQ54,subQ53,subQ52,subQ51,subQ50,subQ49,subQ48,subQ47,subQ46,subQ45,subQ44,subQ43,subQ42,subQ41,subQ40,subQ39,subQ38,subQ37,subQ36,subQ35,subQ34,subQ33,subQ32,subQ31,subQ30,subQ29,subQ28,subQ27,subQ26,subQ25,subQ24,subQ23,subQ22,subQ21,subQ20,subQ19,subQ18,subQ17,subQ16,subQ15,subQ14,subQ13,subQ12,subQ11,subQ10,subQ9,subQ8,subQ7,subQ6,subQ5,subQ4,subQ3,subQ2,subQ1,subQ0]),OD(0.0)],"isStart":false})]});}
            extrude(context, id + "F8", {"entities" : qUnion([Q0, Q1, Q2, Q3]), "operationType" : NewBodyOperationType.ADD, "endBound" : BoundingType.UP_TO_SURFACE, "oppositeDirection" : true, "depth" : 25 * mm, "endBoundEntityFace" : qUnion([Q4]), "offsetDistance" : 25 * mm});
        }
        {
            var Q0;
            Q0=qCreatedBy(makeId("Right.planeOp"),FACE);
            var sketch = newSketch(context, id + "F9", { "sketchPlane" : qUnion([Q0])});
            skLineSegment(sketch, "E248.bottom", {"start": v(-2, 36.23) * mm, "end": v(-1.6, 36.23) * mm});
            skLineSegment(sketch, "E248.top", {"start": v(-2, -95.17) * mm, "end": v(-1.6, -95.17) * mm});
            skLineSegment(sketch, "E248.left", {"start": v(-2, 36.23) * mm, "end": v(-2, -95.17) * mm});
            skLineSegment(sketch, "E248.right", {"start": v(-1.6, 36.23) * mm, "end": v(-1.6, -95.17) * mm});
            skSolve(sketch);
        }
        {
            var Q0;
            Q0 = qSketchRegion(id + "F9", true);
            extrude(context, id + "F10", {"entities" : qUnion([Q0]), "operationType" : NewBodyOperationType.REMOVE, "endBound" : BoundingType.THROUGH_ALL, "oppositeDirection" : true, "depth" : 25 * mm, "offsetDistance" : 25 * mm, "hasSecondDirection" : true, "secondDirectionBound" : SecondDirectionBoundingType.THROUGH_ALL, "secondDirectionOppositeDirection" : false, "secondDirectionDepth" : 25 * mm});
        }
    });